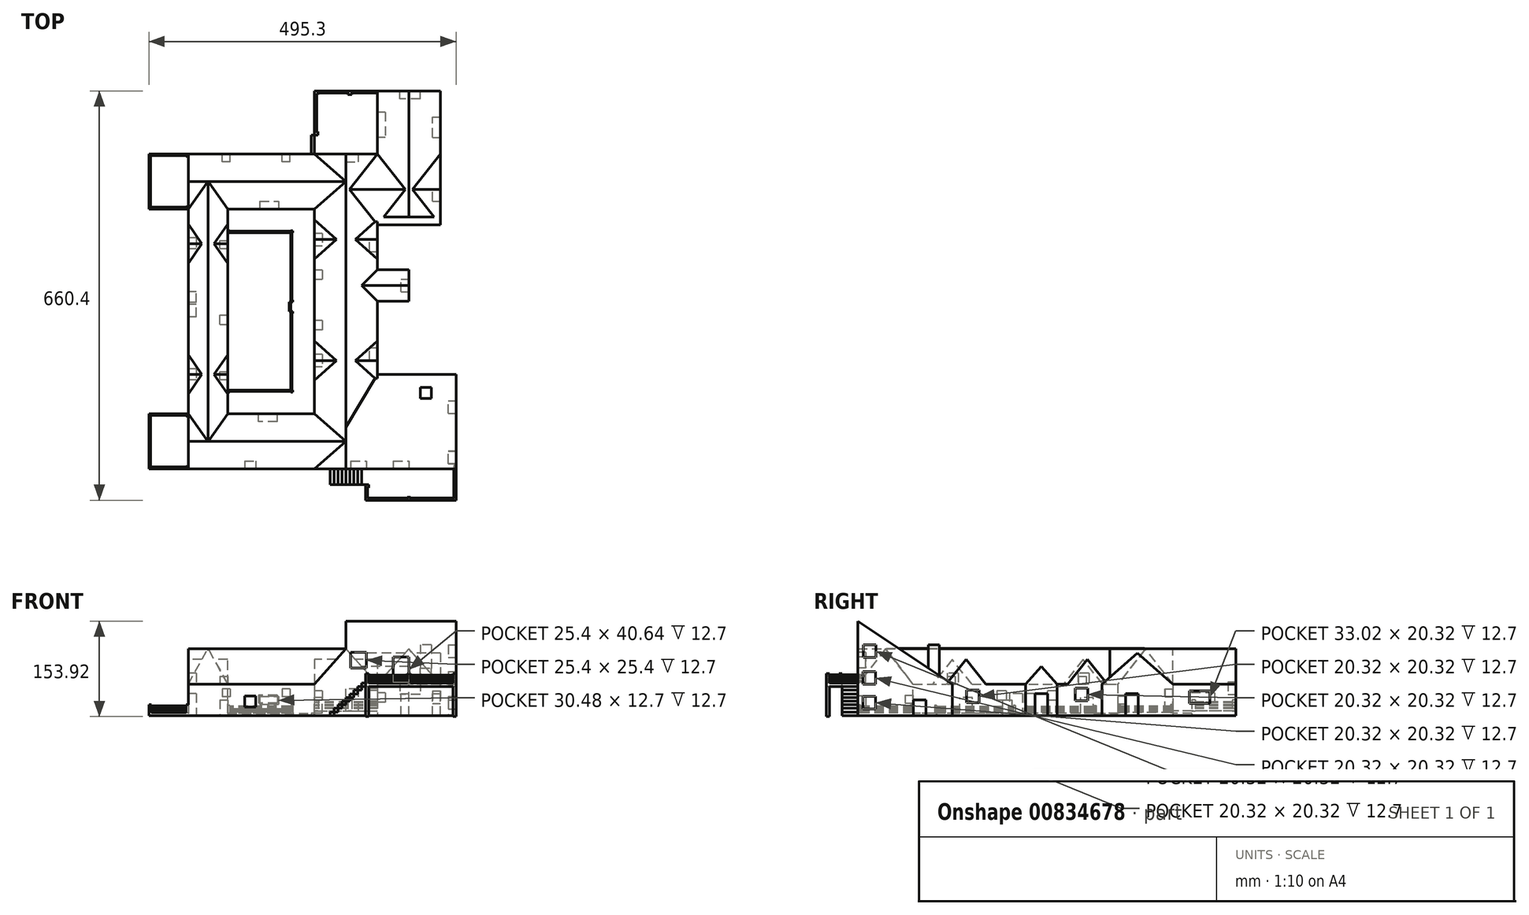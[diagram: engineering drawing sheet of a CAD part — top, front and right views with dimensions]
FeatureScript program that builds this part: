
annotation { "Feature Type Name" : "Feature", "Feature Type Description" : "" }
export const myFeature = defineFeature(function(context is Context, id is Id, definition is map)
    precondition{}
    {
        {
            var Q0;
            Q0=qCreatedBy(makeId("Front.planeOp"),FACE);
            var sketch = newSketch(context, id + "F0", { "sketchPlane" : qUnion([Q0])});
            skLineSegment(sketch, "E0", {"start": v(-50.8, -50.8) * mm, "end": v(50.8, -50.8) * mm});
            skLineSegment(sketch, "E1", {"start": v(50.8, -50.8) * mm, "end": v(50.8, 0) * mm});
            skLineSegment(sketch, "E2", {"start": v(50.8, 0) * mm, "end": v(-50.8, 0) * mm});
            skLineSegment(sketch, "E3", {"start": v(-50.8, 0) * mm, "end": v(-50.8, -50.8) * mm});
            skLineSegment(sketch, "E4", {"start": v(-50.8, 0) * mm, "end": v(0, 56.8) * mm});
            skLineSegment(sketch, "E5", {"start": v(0, 56.8) * mm, "end": v(50.8, 0) * mm});
            skSolve(sketch);
        }
        {
            var Q0;
            Q0=makeQuery(id+"F0.imprint","IMPRINT",FACE,{"disambiguationData":[TD([[makeQuery(id+"F0.imprint","IMPRINT",EDGE,{"derivedFrom":sQuery(id+"F0.wireOp",EDGE,"E2")}),-1.0]])]});
            var Q1;
            Q1=makeQuery(id+"F0.imprint","IMPRINT",FACE,{"disambiguationData":[TD([[makeQuery(id+"F0.imprint","IMPRINT",EDGE,{"derivedFrom":sQuery(id+"F0.wireOp",EDGE,"E0")}),1.0]])]});
            extrude(context, id + "F1", {"entities" : qUnion([Q0, Q1]), "depth" : 508 * mm, "offsetDistance" : 25.4 * mm});
        }
        {
            var Q0;
            Q0=makeQuery(id+"F1.opExtrude","SWEPT_FACE",FACE,{"disambiguationData":[OSD([sQuery(id+"F0.wireOp",EDGE,"E1")])]});
            var sketch = newSketch(context, id + "F2", { "sketchPlane" : qUnion([Q0])});
            skLineSegment(sketch, "E6", {"start": v(-355.6, 0) * mm, "end": v(-508, 0) * mm});
            skLineSegment(sketch, "E7", {"start": v(-355.6, 0) * mm, "end": v(-355.6, -50.8) * mm});
            skLineSegment(sketch, "E8", {"start": v(-355.6, -50.8) * mm, "end": v(-508, -50.8) * mm});
            skLineSegment(sketch, "E9", {"start": v(-508, -50.8) * mm, "end": v(-508, 0) * mm});
            skLineSegment(sketch, "E10", {"start": v(-508, 0) * mm, "end": v(-508, 101.6) * mm});
            skLineSegment(sketch, "E11", {"start": v(-508, 101.6) * mm, "end": v(-355.6, 0) * mm});
            skSolve(sketch);
        }
        {
            var Q0;
            Q0=makeQuery(id+"F2.imprint","IMPRINT",FACE,{"disambiguationData":[TD([[makeQuery(id+"F2.imprint","IMPRINT",EDGE,{"derivedFrom":sQuery(id+"F2.wireOp",EDGE,"E6")}),-1.0]])]});
            var Q1;
            Q1=makeQuery(id+"F2.imprint","IMPRINT",FACE,{"disambiguationData":[TD([[makeQuery(id+"F2.imprint","IMPRINT",EDGE,{"derivedFrom":sQuery(id+"F2.wireOp",EDGE,"iOD2iBbH-JStM-AViZ-ixR9-aIs0KOxaWcK1")}),-1.0]])]});
            extrude(context, id + "F3", {"entities" : qUnion([Q0, Q1]), "operationType" : NewBodyOperationType.ADD, "depth" : 127 * mm, "offsetDistance" : 25.4 * mm});
        }
        {
            var Q0;
            Q0=makeQuery(id+"F2.imprint","IMPRINT",FACE,{"disambiguationData":[TD([[makeQuery(id+"F2.imprint","IMPRINT",EDGE,{"derivedFrom":sQuery(id+"F2.wireOp",EDGE,"E6")}),1.0]])]});
            extrude(context, id + "F4", {"entities" : qUnion([Q0]), "operationType" : NewBodyOperationType.ADD, "depth" : 127 * mm, "offsetDistance" : 25.4 * mm});
        }
        {
            var Q0;
            Q0=makeQuery(id+"F4.opExtrude","CAP_FACE",FACE,{"disambiguationData":[OSD([sQuery(id+"F2.wireOp",EDGE,"E6"),sQuery(id+"F2.wireOp",EDGE,"E10"),sQuery(id+"F2.wireOp",EDGE,"E11")])],"isStart":true});
            extrude(context, id + "F5", {"entities" : qUnion([Q0]), "operationType" : NewBodyOperationType.ADD, "depth" : 50.8 * mm, "offsetDistance" : 25.4 * mm});
        }
        {
            var Q0;
            Q0=makeQuery(id+"F1.opExtrude","SWEPT_FACE",FACE,{"disambiguationData":[OSD([sQuery(id+"F0.wireOp",EDGE,"E1")])]});
            var sketch = newSketch(context, id + "F6", { "sketchPlane" : qUnion([Q0])});
            skLineSegment(sketch, "E12.bottom", {"start": v(-237.52, -50.8) * mm, "end": v(-186.72, -50.8) * mm});
            skLineSegment(sketch, "E12.top", {"start": v(-237.52, 0) * mm, "end": v(-186.72, 0) * mm});
            skLineSegment(sketch, "E12.left", {"start": v(-237.52, -50.8) * mm, "end": v(-237.52, 0) * mm});
            skLineSegment(sketch, "E12.right", {"start": v(-186.72, -50.8) * mm, "end": v(-186.72, 0) * mm});
            skLineSegment(sketch, "E13", {"start": v(-237.52, 0) * mm, "end": v(-212.12, 28.4) * mm});
            skPoint(sketch, "E13.endSnap0", {"position": v(-212.12, 0) * mm});
            skLineSegment(sketch, "E14", {"start": v(-212.12, 28.4) * mm, "end": v(-186.72, 0) * mm});
            skSolve(sketch);
        }
        {
            var Q0;
            Q0=makeQuery(id+"F6.imprint","IMPRINT",FACE,{"disambiguationData":[TD([[makeQuery(id+"F6.imprint","IMPRINT",EDGE,{"derivedFrom":sQuery(id+"F6.wireOp",EDGE,"E12.bottom")}),1.0]])]});
            var Q1;
            Q1=makeQuery(id+"F6.imprint","IMPRINT",FACE,{"disambiguationData":[TD([[makeQuery(id+"F6.imprint","IMPRINT",EDGE,{"derivedFrom":sQuery(id+"F6.wireOp",EDGE,"E12.top")}),1.0]])]});
            extrude(context, id + "F7", {"entities" : qUnion([Q0, Q1]), "operationType" : NewBodyOperationType.ADD, "depth" : 50.8 * mm, "offsetDistance" : 25.4 * mm});
        }
        {
            var Q0;
            Q0=makeQuery(id+"F7.opExtrude","CAP_FACE",FACE,{"disambiguationData":[OSD([sQuery(id+"F6.wireOp",EDGE,"E12.bottom"),sQuery(id+"F6.wireOp",EDGE,"E12.left"),sQuery(id+"F6.wireOp",EDGE,"E12.right"),sQuery(id+"F6.wireOp",EDGE,"E13"),sQuery(id+"F6.wireOp",EDGE,"E14")])],"isStart":true});
            extrude(context, id + "F8", {"entities" : qUnion([Q0]), "operationType" : NewBodyOperationType.ADD, "depth" : 25.4 * mm, "offsetDistance" : 25.4 * mm});
        }
        {
            var Q0;
            {var subQ2=sQuery(id+"F0.wireOp",EDGE,"E1");var subQ4=sQuery(id+"F6.wireOp",EDGE,"E12.right");Q0=makeQuery(id+"F7.boolean.opBoolean","SPLIT",FACE,{"disambiguationData":[TD([makeQuery(id+"F7.opExtrude","SWEPT_FACE",FACE,{"disambiguationData":[OSD([subQ4])]})])],"derivedFrom":makeQuery(id+"F1.opExtrude","SWEPT_FACE",FACE,{"disambiguationData":[OSD([subQ2])]})});}
            var sketch = newSketch(context, id + "F9", { "sketchPlane" : qUnion([Q0])});
            skLineSegment(sketch, "E15.bottom", {"start": v(-114.3, 0) * mm, "end": v(0, 0) * mm});
            skLineSegment(sketch, "E15.top", {"start": v(-114.3, -50.8) * mm, "end": v(0, -50.8) * mm});
            skLineSegment(sketch, "E15.left", {"start": v(-114.3, 0) * mm, "end": v(-114.3, -50.8) * mm});
            skLineSegment(sketch, "E15.right", {"start": v(0, 0) * mm, "end": v(0, -50.8) * mm});
            skLineSegment(sketch, "E16", {"start": v(-114.3, 0) * mm, "end": v(-57.15, 50.4) * mm});
            skPoint(sketch, "E16.endSnap0", {"position": v(-57.15, 0) * mm});
            skLineSegment(sketch, "E17", {"start": v(-57.15, 50.4) * mm, "end": v(0, 0) * mm});
            skSolve(sketch);
        }
        {
            var Q0;
            Q0=makeQuery(id+"F9.imprint","IMPRINT",FACE,{"disambiguationData":[TD([[makeQuery(id+"F9.imprint","IMPRINT",EDGE,{"derivedFrom":sQuery(id+"F9.wireOp",EDGE,"E15.bottom")}),1.0]])]});
            var Q1;
            Q1=makeQuery(id+"F9.imprint","IMPRINT",FACE,{"disambiguationData":[TD([[makeQuery(id+"F9.imprint","IMPRINT",EDGE,{"derivedFrom":sQuery(id+"F9.wireOp",EDGE,"E15.bottom")}),-1.0]])]});
            extrude(context, id + "F10", {"entities" : qUnion([Q0, Q1]), "operationType" : NewBodyOperationType.ADD, "depth" : 101.6 * mm, "offsetDistance" : 25.4 * mm});
        }
        {
            var Q0;
            Q0=makeQuery(id+"F10.opExtrude","CAP_FACE",FACE,{"disambiguationData":[OSD([sQuery(id+"F9.wireOp",EDGE,"E15.top"),sQuery(id+"F9.wireOp",EDGE,"E15.left"),sQuery(id+"F9.wireOp",EDGE,"E15.right"),sQuery(id+"F9.wireOp",EDGE,"E16"),sQuery(id+"F9.wireOp",EDGE,"E17")])],"isStart":true});
            extrude(context, id + "F11", {"entities" : qUnion([Q0]), "operationType" : NewBodyOperationType.ADD, "depth" : 50.8 * mm, "offsetDistance" : 25.4 * mm});
        }
        {
            var Q0;
            Q0=makeQuery(id+"F10.boolean.opBoolean","MERGE",FACE,{"derivedFrom":[makeQuery(id+"F1.opExtrude","CAP_FACE",FACE,{"disambiguationData":[OSD([sQuery(id+"F0.wireOp",EDGE,"E0"),sQuery(id+"F0.wireOp",EDGE,"E1"),sQuery(id+"F0.wireOp",EDGE,"E3"),sQuery(id+"F0.wireOp",EDGE,"E4"),sQuery(id+"F0.wireOp",EDGE,"E5")])],"isStart":true}),makeQuery(id+"F10.opExtrude","SWEPT_FACE",FACE,{"disambiguationData":[OSD([sQuery(id+"F9.wireOp",EDGE,"E15.right")])]})]});
            var sketch = newSketch(context, id + "F12", { "sketchPlane" : qUnion([Q0])});
            skLineSegment(sketch, "E18.bottom", {"start": v(-50.8, 0) * mm, "end": v(-152.4, 0) * mm});
            skLineSegment(sketch, "E18.top", {"start": v(-50.8, -50.8) * mm, "end": v(-152.4, -50.8) * mm});
            skLineSegment(sketch, "E18.left", {"start": v(-50.8, 0) * mm, "end": v(-50.8, -50.8) * mm});
            skLineSegment(sketch, "E18.right", {"start": v(-152.4, 0) * mm, "end": v(-152.4, -50.8) * mm});
            skLineSegment(sketch, "E19", {"start": v(-152.4, 0) * mm, "end": v(-101.6, 56.8) * mm});
            skPoint(sketch, "E19.endSnap0", {"position": v(-101.6, 0) * mm});
            skLineSegment(sketch, "E20", {"start": v(-101.6, 56.8) * mm, "end": v(-50.8, 0) * mm});
            skSolve(sketch);
        }
        {
            var Q0;
            Q0=makeQuery(id+"F12.imprint","IMPRINT",FACE,{"disambiguationData":[TD([[makeQuery(id+"F12.imprint","IMPRINT",EDGE,{"derivedFrom":sQuery(id+"F12.wireOp",EDGE,"E18.bottom")}),-1.0]])]});
            var Q1;
            Q1=makeQuery(id+"F12.imprint","IMPRINT",FACE,{"disambiguationData":[TD([[makeQuery(id+"F12.imprint","IMPRINT",EDGE,{"derivedFrom":sQuery(id+"F12.wireOp",EDGE,"E18.bottom")}),1.0]])]});
            extrude(context, id + "F13", {"entities" : qUnion([Q0, Q1]), "operationType" : NewBodyOperationType.ADD, "depth" : 101.6 * mm, "offsetDistance" : 25.4 * mm});
        }
        {
            var Q0;
            Q0=makeQuery(id+"F13.opExtrude","CAP_FACE",FACE,{"disambiguationData":[OSD([sQuery(id+"F12.wireOp",EDGE,"E18.top"),sQuery(id+"F12.wireOp",EDGE,"E18.left"),sQuery(id+"F12.wireOp",EDGE,"E18.right"),sQuery(id+"F12.wireOp",EDGE,"E19"),sQuery(id+"F12.wireOp",EDGE,"E20")])],"isStart":true});
            extrude(context, id + "F14", {"entities" : qUnion([Q0]), "operationType" : NewBodyOperationType.ADD, "depth" : 101.6 * mm, "offsetDistance" : 25.4 * mm});
        }
        {
            var Q0;
            Q0=makeQuery(id+"F1.opExtrude","SWEPT_FACE",FACE,{"disambiguationData":[OSD([sQuery(id+"F0.wireOp",EDGE,"E3")])]});
            var sketch = newSketch(context, id + "F15", { "sketchPlane" : qUnion([Q0])});
            skLineSegment(sketch, "E21.bottom", {"start": v(0, 0) * mm, "end": v(88.9, 0) * mm});
            skLineSegment(sketch, "E21.top", {"start": v(0, -50.8) * mm, "end": v(88.9, -50.8) * mm});
            skLineSegment(sketch, "E21.left", {"start": v(0, 0) * mm, "end": v(0, -50.8) * mm});
            skLineSegment(sketch, "E21.right", {"start": v(88.9, 0) * mm, "end": v(88.9, -50.8) * mm});
            skLineSegment(sketch, "E22", {"start": v(0, 0) * mm, "end": v(44.45, 56.81) * mm});
            skPoint(sketch, "E22.endSnap0", {"position": v(44.45, 0) * mm});
            skLineSegment(sketch, "E23", {"start": v(44.45, 56.81) * mm, "end": v(88.9, 0) * mm});
            skLineSegment(sketch, "E24.bottom", {"start": v(508, 0) * mm, "end": v(419.1, 0) * mm});
            skLineSegment(sketch, "E24.top", {"start": v(508, -50.8) * mm, "end": v(419.1, -50.8) * mm});
            skLineSegment(sketch, "E24.left", {"start": v(508, 0) * mm, "end": v(508, -50.8) * mm});
            skLineSegment(sketch, "E24.right", {"start": v(419.1, 0) * mm, "end": v(419.1, -50.8) * mm});
            skLineSegment(sketch, "E25", {"start": v(419.1, 0) * mm, "end": v(463.55, 56.81) * mm});
            skPoint(sketch, "E25.endSnap0", {"position": v(463.55, 0) * mm});
            skLineSegment(sketch, "E26", {"start": v(463.55, 56.81) * mm, "end": v(508, 0) * mm});
            skSolve(sketch);
        }
        {
            var Q0;
            Q0=makeQuery(id+"F15.imprint","IMPRINT",FACE,{"disambiguationData":[TD([[makeQuery(id+"F15.imprint","IMPRINT",EDGE,{"derivedFrom":sQuery(id+"F15.wireOp",EDGE,"E21.bottom")}),1.0]])]});
            var Q1;
            Q1=makeQuery(id+"F15.imprint","IMPRINT",FACE,{"disambiguationData":[TD([[makeQuery(id+"F15.imprint","IMPRINT",EDGE,{"derivedFrom":sQuery(id+"F15.wireOp",EDGE,"E21.bottom")}),-1.0]])]});
            var Q2;
            Q2=makeQuery(id+"F15.imprint","IMPRINT",FACE,{"disambiguationData":[TD([[makeQuery(id+"F15.imprint","IMPRINT",EDGE,{"derivedFrom":sQuery(id+"F15.wireOp",EDGE,"E24.bottom")}),1.0]])]});
            var Q3;
            Q3=makeQuery(id+"F15.imprint","IMPRINT",FACE,{"disambiguationData":[TD([[makeQuery(id+"F15.imprint","IMPRINT",EDGE,{"derivedFrom":sQuery(id+"F15.wireOp",EDGE,"E24.bottom")}),-1.0]])]});
            extrude(context, id + "F16", {"entities" : qUnion([Q0, Q1, Q2, Q3]), "operationType" : NewBodyOperationType.ADD, "depth" : 203.2 * mm, "offsetDistance" : 25.4 * mm});
        }
        {
            var Q0;
            Q0=makeQuery(id+"F16.opExtrude","CAP_FACE",FACE,{"disambiguationData":[OSD([sQuery(id+"F15.wireOp",EDGE,"E21.top"),sQuery(id+"F15.wireOp",EDGE,"E21.left"),sQuery(id+"F15.wireOp",EDGE,"E21.right"),sQuery(id+"F15.wireOp",EDGE,"E22"),sQuery(id+"F15.wireOp",EDGE,"E23")])],"isStart":true});
            extrude(context, id + "F17", {"entities" : qUnion([Q0]), "operationType" : NewBodyOperationType.ADD, "depth" : 50.8 * mm, "offsetDistance" : 25.4 * mm});
        }
        {
            var Q0;
            Q0=makeQuery(id+"F16.opExtrude","CAP_FACE",FACE,{"disambiguationData":[OSD([sQuery(id+"F15.wireOp",EDGE,"E24.top"),sQuery(id+"F15.wireOp",EDGE,"E24.left"),sQuery(id+"F15.wireOp",EDGE,"E24.right"),sQuery(id+"F15.wireOp",EDGE,"E25"),sQuery(id+"F15.wireOp",EDGE,"E26")])],"isStart":true});
            extrude(context, id + "F18", {"entities" : qUnion([Q0]), "operationType" : NewBodyOperationType.ADD, "depth" : 50.8 * mm, "offsetDistance" : 25.4 * mm});
        }
        {
            var Q0;
            Q0=makeQuery(id+"F16.opExtrude","SWEPT_FACE",FACE,{"disambiguationData":[OSD([sQuery(id+"F15.wireOp",EDGE,"E21.right")])]});
            var sketch = newSketch(context, id + "F19", { "sketchPlane" : qUnion([Q0])});
            skLineSegment(sketch, "E27.bottom", {"start": v(-190.5, 0) * mm, "end": v(-254, 0) * mm});
            skLineSegment(sketch, "E27.top", {"start": v(-190.5, -50.8) * mm, "end": v(-254, -50.8) * mm});
            skLineSegment(sketch, "E27.left", {"start": v(-190.5, 0) * mm, "end": v(-190.5, -50.8) * mm});
            skLineSegment(sketch, "E27.right", {"start": v(-254, 0) * mm, "end": v(-254, -50.8) * mm});
            skLineSegment(sketch, "E28", {"start": v(-254, 0) * mm, "end": v(-222.25, 57.62) * mm});
            skPoint(sketch, "E28.endSnap0", {"position": v(-222.25, 0) * mm});
            skLineSegment(sketch, "E29", {"start": v(-222.25, 57.62) * mm, "end": v(-190.5, 0) * mm});
            skSolve(sketch);
        }
        {
            var Q0;
            Q0=makeQuery(id+"F19.imprint","IMPRINT",FACE,{"disambiguationData":[TD([[makeQuery(id+"F19.imprint","IMPRINT",EDGE,{"derivedFrom":sQuery(id+"F19.wireOp",EDGE,"E27.bottom")}),-1.0]])]});
            var Q1;
            Q1=makeQuery(id+"F19.imprint","IMPRINT",FACE,{"disambiguationData":[TD([[makeQuery(id+"F19.imprint","IMPRINT",EDGE,{"derivedFrom":sQuery(id+"F19.wireOp",EDGE,"E27.bottom")}),1.0]])]});
            extrude(context, id + "F20", {"entities" : qUnion([Q0, Q1]), "operationType" : NewBodyOperationType.ADD, "depth" : 355.6 * mm, "offsetDistance" : 25.4 * mm});
        }
        {
            var Q0;
            Q0=makeQuery(id+"F20.opExtrude","CAP_FACE",FACE,{"disambiguationData":[OSD([sQuery(id+"F19.wireOp",EDGE,"E27.top"),sQuery(id+"F19.wireOp",EDGE,"E27.left"),sQuery(id+"F19.wireOp",EDGE,"E27.right"),sQuery(id+"F19.wireOp",EDGE,"E28"),sQuery(id+"F19.wireOp",EDGE,"E29")])],"isStart":false});
            extrude(context, id + "F21", {"entities" : qUnion([Q0]), "operationType" : NewBodyOperationType.ADD, "depth" : 17.78 * mm, "offsetDistance" : 25.4 * mm});
        }
        {
            var Q0;
            Q0=makeQuery(id+"F20.opExtrude","CAP_FACE",FACE,{"disambiguationData":[OSD([sQuery(id+"F19.wireOp",EDGE,"E27.top"),sQuery(id+"F19.wireOp",EDGE,"E27.left"),sQuery(id+"F19.wireOp",EDGE,"E27.right"),sQuery(id+"F19.wireOp",EDGE,"E28"),sQuery(id+"F19.wireOp",EDGE,"E29")])],"isStart":true});
            extrude(context, id + "F22", {"entities" : qUnion([Q0]), "operationType" : NewBodyOperationType.ADD, "depth" : 43.18 * mm, "offsetDistance" : 25.4 * mm});
        }
        {
            var Q0;
            Q0=makeQuery(id+"F1.opExtrude","SWEPT_FACE",FACE,{"disambiguationData":[OSD([sQuery(id+"F0.wireOp",EDGE,"E3")])]});
            var sketch = newSketch(context, id + "F23", { "sketchPlane" : qUnion([Q0])});
            skLineSegment(sketch, "E30", {"start": v(106.35, 0) * mm, "end": v(138.1, 39.66) * mm});
            skLineSegment(sketch, "E31", {"start": v(138.1, 39.66) * mm, "end": v(169.85, 0) * mm});
            skLineSegment(sketch, "E32", {"start": v(169.85, 0) * mm, "end": v(106.35, 0) * mm});
            skLineSegment(sketch, "E33", {"start": v(301.86, 0) * mm, "end": v(333.61, 39.66) * mm});
            skLineSegment(sketch, "E34", {"start": v(333.61, 39.66) * mm, "end": v(365.36, 0) * mm});
            skLineSegment(sketch, "E35", {"start": v(365.36, 0) * mm, "end": v(301.86, 0) * mm});
            skSolve(sketch);
        }
        {
            var Q0;
            Q0=makeQuery(id+"F23.imprint","IMPRINT",FACE,{"disambiguationData":[TD([[makeQuery(id+"F23.imprint","IMPRINT",EDGE,{"derivedFrom":sQuery(id+"F23.wireOp",EDGE,"E30")}),-1.0]])]});
            var Q1;
            Q1=makeQuery(id+"F23.imprint","IMPRINT",FACE,{"disambiguationData":[TD([[makeQuery(id+"F23.imprint","IMPRINT",EDGE,{"derivedFrom":sQuery(id+"F23.wireOp",EDGE,"E33")}),-1.0]])]});
            extrude(context, id + "F24", {"entities" : qUnion([Q0, Q1]), "operationType" : NewBodyOperationType.ADD, "oppositeDirection" : true, "depth" : 101.6 * mm, "offsetDistance" : 25.4 * mm});
        }
        {
            var Q0;
            Q0=makeQuery(id+"F20.boolean.opBoolean","MERGE",FACE,{"derivedFrom":[makeQuery(id+"F16.opExtrude","CAP_FACE",FACE,{"disambiguationData":[OSD([sQuery(id+"F15.wireOp",EDGE,"E21.top"),sQuery(id+"F15.wireOp",EDGE,"E21.left"),sQuery(id+"F15.wireOp",EDGE,"E21.right"),sQuery(id+"F15.wireOp",EDGE,"E22"),sQuery(id+"F15.wireOp",EDGE,"E23")])],"isStart":false}),makeQuery(id+"F16.opExtrude","CAP_FACE",FACE,{"disambiguationData":[OSD([sQuery(id+"F15.wireOp",EDGE,"E24.top"),sQuery(id+"F15.wireOp",EDGE,"E24.left"),sQuery(id+"F15.wireOp",EDGE,"E24.right"),sQuery(id+"F15.wireOp",EDGE,"E25"),sQuery(id+"F15.wireOp",EDGE,"E26")])],"isStart":false}),makeQuery(id+"F20.opExtrude","SWEPT_FACE",FACE,{"disambiguationData":[OSD([sQuery(id+"F19.wireOp",EDGE,"E27.right")])]})]});
            var sketch = newSketch(context, id + "F25", { "sketchPlane" : qUnion([Q0])});
            skLineSegment(sketch, "E36", {"start": v(113.08, 0) * mm, "end": v(144.83, 39.66) * mm});
            skLineSegment(sketch, "E37", {"start": v(144.83, 39.66) * mm, "end": v(176.58, 0) * mm});
            skLineSegment(sketch, "E38", {"start": v(176.58, 0) * mm, "end": v(113.08, 0) * mm});
            skLineSegment(sketch, "E39", {"start": v(324.16, 0) * mm, "end": v(355.91, 39.66) * mm});
            skLineSegment(sketch, "E40", {"start": v(355.91, 39.66) * mm, "end": v(387.66, 0) * mm});
            skLineSegment(sketch, "E41", {"start": v(387.66, 0) * mm, "end": v(324.16, 0) * mm});
            skSolve(sketch);
        }
        {
            var Q0;
            Q0=makeQuery(id+"F25.imprint","IMPRINT",FACE,{"disambiguationData":[TD([[makeQuery(id+"F25.imprint","IMPRINT",EDGE,{"derivedFrom":sQuery(id+"F25.wireOp",EDGE,"E36")}),-1.0]])]});
            var Q1;
            Q1=makeQuery(id+"F25.imprint","IMPRINT",FACE,{"disambiguationData":[TD([[makeQuery(id+"F25.imprint","IMPRINT",EDGE,{"derivedFrom":sQuery(id+"F25.wireOp",EDGE,"E39")}),-1.0]])]});
            extrude(context, id + "F26", {"entities" : qUnion([Q0, Q1]), "operationType" : NewBodyOperationType.ADD, "oppositeDirection" : true, "depth" : 63.5 * mm, "offsetDistance" : 25.4 * mm});
        }
        {
            var Q0;
            Q0=makeQuery(id+"F13.opExtrude","SWEPT_FACE",FACE,{"disambiguationData":[OSD([sQuery(id+"F12.wireOp",EDGE,"E18.left")])]});
            var sketch = newSketch(context, id + "F27", { "sketchPlane" : qUnion([Q0])});
            skLineSegment(sketch, "E42.bottom", {"start": v(-101.6, -43.18) * mm, "end": v(0, -43.18) * mm});
            skLineSegment(sketch, "E42.top", {"start": v(-101.6, -50.8) * mm, "end": v(0, -50.8) * mm});
            skLineSegment(sketch, "E42.left", {"start": v(-101.6, -43.18) * mm, "end": v(-101.6, -50.8) * mm});
            skLineSegment(sketch, "E42.right", {"start": v(0, -43.18) * mm, "end": v(0, -50.8) * mm});
            skSolve(sketch);
        }
        {
            var Q0;
            Q0=makeQuery(id+"F27.imprint","IMPRINT",FACE,{"disambiguationData":[TD([[makeQuery(id+"F27.imprint","IMPRINT",EDGE,{"derivedFrom":sQuery(id+"F27.wireOp",EDGE,"E42.bottom")}),-1.0]])]});
            extrude(context, id + "F28", {"entities" : qUnion([Q0]), "operationType" : NewBodyOperationType.ADD, "depth" : 101.6 * mm, "offsetDistance" : 25.4 * mm});
        }
        {
            var Q0;
            Q0=makeQuery(id+"F28.opExtrude","SWEPT_FACE",FACE,{"disambiguationData":[OSD([sQuery(id+"F27.wireOp",EDGE,"E42.bottom")])]});
            var sketch = newSketch(context, id + "F29", { "sketchPlane" : qUnion([Q0])});
            skLineSegment(sketch, "E43.bottom", {"start": v(-44.7, 101.6) * mm, "end": v(-50.8, 101.6) * mm});
            skLineSegment(sketch, "E43.top", {"start": v(-44.7, 96.01) * mm, "end": v(-50.8, 96.01) * mm});
            skLineSegment(sketch, "E43.left", {"start": v(-44.7, 101.6) * mm, "end": v(-44.7, 96.01) * mm});
            skLineSegment(sketch, "E43.right", {"start": v(-50.8, 101.6) * mm, "end": v(-50.8, 96.01) * mm});
            skLineSegment(sketch, "E44.bottom", {"start": v(-50.8, 30.52) * mm, "end": v(-44.7, 30.52) * mm});
            skLineSegment(sketch, "E44.top", {"start": v(-50.8, 36.1) * mm, "end": v(-44.7, 36.1) * mm});
            skLineSegment(sketch, "E44.left", {"start": v(-50.8, 30.52) * mm, "end": v(-50.8, 36.1) * mm});
            skLineSegment(sketch, "E44.right", {"start": v(-44.7, 30.52) * mm, "end": v(-44.7, 36.1) * mm});
            skLineSegment(sketch, "E45.bottom", {"start": v(9.73, 96.01) * mm, "end": v(3.63, 96.01) * mm});
            skLineSegment(sketch, "E45.top", {"start": v(9.73, 101.6) * mm, "end": v(3.63, 101.6) * mm});
            skLineSegment(sketch, "E45.left", {"start": v(9.73, 96.01) * mm, "end": v(9.73, 101.6) * mm});
            skLineSegment(sketch, "E45.right", {"start": v(3.63, 96.01) * mm, "end": v(3.63, 101.6) * mm});
            skSolve(sketch);
        }
        {
            var Q0;
            Q0=makeQuery(id+"F29.imprint","IMPRINT",FACE,{"disambiguationData":[TD([[makeQuery(id+"F29.imprint","IMPRINT",EDGE,{"derivedFrom":sQuery(id+"F29.wireOp",EDGE,"E44.bottom")}),1.0]])]});
            var Q1;
            Q1=makeQuery(id+"F29.imprint","IMPRINT",FACE,{"disambiguationData":[TD([[makeQuery(id+"F29.imprint","IMPRINT",EDGE,{"derivedFrom":sQuery(id+"F29.wireOp",EDGE,"E43.bottom")}),-1.0]])]});
            var Q2;
            Q2=makeQuery(id+"F29.imprint","IMPRINT",FACE,{"disambiguationData":[TD([[makeQuery(id+"F29.imprint","IMPRINT",EDGE,{"derivedFrom":sQuery(id+"F29.wireOp",EDGE,"E45.bottom")}),-1.0]])]});
            extrude(context, id + "F30", {"entities" : qUnion([Q0, Q1, Q2]), "operationType" : NewBodyOperationType.ADD, "depth" : 17.78 * mm, "offsetDistance" : 25.4 * mm});
        }
        {
            var Q0;
            Q0=makeQuery(id+"F30.opExtrude","SWEPT_FACE",FACE,{"disambiguationData":[OSD([sQuery(id+"F29.wireOp",EDGE,"E44.top")])]});
            var sketch = newSketch(context, id + "F31", { "sketchPlane" : qUnion([Q0])});
            skLineSegment(sketch, "E46.bottom", {"start": v(46.74, -28.7) * mm, "end": v(48.26, -28.7) * mm});
            skLineSegment(sketch, "E46.top", {"start": v(46.74, -30.1) * mm, "end": v(48.26, -30.1) * mm});
            skLineSegment(sketch, "E46.left", {"start": v(46.74, -28.7) * mm, "end": v(46.74, -30.1) * mm});
            skLineSegment(sketch, "E46.right", {"start": v(48.26, -28.7) * mm, "end": v(48.26, -30.1) * mm});
            skLineSegment(sketch, "E47.bottom", {"start": v(46.74, -33.4) * mm, "end": v(48.26, -33.4) * mm});
            skLineSegment(sketch, "E47.top", {"start": v(46.74, -34.8) * mm, "end": v(48.26, -34.8) * mm});
            skLineSegment(sketch, "E47.left", {"start": v(46.74, -33.4) * mm, "end": v(46.74, -34.8) * mm});
            skLineSegment(sketch, "E47.right", {"start": v(48.26, -33.4) * mm, "end": v(48.26, -34.8) * mm});
            skLineSegment(sketch, "E48.bottom", {"start": v(46.74, -38.1) * mm, "end": v(48.26, -38.1) * mm});
            skLineSegment(sketch, "E48.top", {"start": v(46.74, -39.5) * mm, "end": v(48.26, -39.5) * mm});
            skLineSegment(sketch, "E48.left", {"start": v(46.74, -38.1) * mm, "end": v(46.74, -39.5) * mm});
            skLineSegment(sketch, "E48.right", {"start": v(48.26, -38.1) * mm, "end": v(48.26, -39.5) * mm});
            skSolve(sketch);
        }
        {
            var Q0;
            Q0=makeQuery(id+"F31.imprint","IMPRINT",FACE,{"disambiguationData":[TD([[makeQuery(id+"F31.imprint","IMPRINT",EDGE,{"derivedFrom":sQuery(id+"F31.wireOp",EDGE,"E48.bottom")}),-1.0]])]});
            var Q1;
            Q1=makeQuery(id+"F31.imprint","IMPRINT",FACE,{"disambiguationData":[TD([[makeQuery(id+"F31.imprint","IMPRINT",EDGE,{"derivedFrom":sQuery(id+"F31.wireOp",EDGE,"E47.bottom")}),-1.0]])]});
            var Q2;
            Q2=makeQuery(id+"F31.imprint","IMPRINT",FACE,{"disambiguationData":[TD([[makeQuery(id+"F31.imprint","IMPRINT",EDGE,{"derivedFrom":sQuery(id+"F31.wireOp",EDGE,"E46.bottom")}),-1.0]])]});
            extrude(context, id + "F32", {"entities" : qUnion([Q0, Q1, Q2]), "operationType" : NewBodyOperationType.ADD, "depth" : 63.5 * mm, "offsetDistance" : 25.4 * mm});
        }
        {
            var Q0;
            Q0=makeQuery(id+"F30.opExtrude","SWEPT_FACE",FACE,{"disambiguationData":[OSD([sQuery(id+"F29.wireOp",EDGE,"E43.left")])]});
            var sketch = newSketch(context, id + "F33", { "sketchPlane" : qUnion([Q0])});
            skLineSegment(sketch, "E49.bottom", {"start": v(98.04, -33.4) * mm, "end": v(99.57, -33.4) * mm});
            skLineSegment(sketch, "E49.top", {"start": v(98.04, -34.8) * mm, "end": v(99.57, -34.8) * mm});
            skLineSegment(sketch, "E49.left", {"start": v(98.04, -33.4) * mm, "end": v(98.04, -34.8) * mm});
            skLineSegment(sketch, "E49.right", {"start": v(99.57, -33.4) * mm, "end": v(99.57, -34.8) * mm});
            skLineSegment(sketch, "E50.bottom", {"start": v(98.04, -38.1) * mm, "end": v(99.57, -38.1) * mm});
            skLineSegment(sketch, "E50.top", {"start": v(98.04, -39.5) * mm, "end": v(99.57, -39.5) * mm});
            skLineSegment(sketch, "E50.left", {"start": v(98.04, -38.1) * mm, "end": v(98.04, -39.5) * mm});
            skLineSegment(sketch, "E50.right", {"start": v(99.57, -38.1) * mm, "end": v(99.57, -39.5) * mm});
            skLineSegment(sketch, "E51.bottom", {"start": v(98.04, -28.7) * mm, "end": v(99.57, -28.7) * mm});
            skLineSegment(sketch, "E51.top", {"start": v(98.04, -30.1) * mm, "end": v(99.57, -30.1) * mm});
            skLineSegment(sketch, "E51.left", {"start": v(98.04, -28.7) * mm, "end": v(98.04, -30.1) * mm});
            skLineSegment(sketch, "E51.right", {"start": v(99.57, -28.7) * mm, "end": v(99.57, -30.1) * mm});
            skSolve(sketch);
        }
        {
            var Q0;
            Q0=makeQuery(id+"F33.imprint","IMPRINT",FACE,{"disambiguationData":[TD([[makeQuery(id+"F33.imprint","IMPRINT",EDGE,{"derivedFrom":sQuery(id+"F33.wireOp",EDGE,"E51.bottom")}),-1.0]])]});
            var Q1;
            Q1=makeQuery(id+"F33.imprint","IMPRINT",FACE,{"disambiguationData":[TD([[makeQuery(id+"F33.imprint","IMPRINT",EDGE,{"derivedFrom":sQuery(id+"F33.wireOp",EDGE,"E49.bottom")}),-1.0]])]});
            var Q2;
            Q2=makeQuery(id+"F33.imprint","IMPRINT",FACE,{"disambiguationData":[TD([[makeQuery(id+"F33.imprint","IMPRINT",EDGE,{"derivedFrom":sQuery(id+"F33.wireOp",EDGE,"E50.bottom")}),-1.0]])]});
            extrude(context, id + "F34", {"entities" : qUnion([Q0, Q1, Q2]), "operationType" : NewBodyOperationType.ADD, "depth" : 127 * mm, "offsetDistance" : 25.4 * mm});
        }
        {
            var Q0;
            Q0=makeQuery(id+"F16.boolean.opBoolean","MERGE",FACE,{"derivedFrom":[makeQuery(id+"F10.boolean.opBoolean","MERGE",FACE,{"derivedFrom":[makeQuery(id+"F1.opExtrude","CAP_FACE",FACE,{"disambiguationData":[OSD([sQuery(id+"F0.wireOp",EDGE,"E0"),sQuery(id+"F0.wireOp",EDGE,"E1"),sQuery(id+"F0.wireOp",EDGE,"E3"),sQuery(id+"F0.wireOp",EDGE,"E4"),sQuery(id+"F0.wireOp",EDGE,"E5")])],"isStart":true}),makeQuery(id+"F10.opExtrude","SWEPT_FACE",FACE,{"disambiguationData":[OSD([sQuery(id+"F9.wireOp",EDGE,"E15.right")])]})]}),makeQuery(id+"F16.opExtrude","SWEPT_FACE",FACE,{"disambiguationData":[OSD([sQuery(id+"F15.wireOp",EDGE,"E21.left")])]})]});
            var sketch = newSketch(context, id + "F35", { "sketchPlane" : qUnion([Q0])});
            skLineSegment(sketch, "E52.bottom", {"start": v(50.8, -46.99) * mm, "end": v(55.88, -46.99) * mm});
            skLineSegment(sketch, "E52.top", {"start": v(50.8, -50.8) * mm, "end": v(55.88, -50.8) * mm});
            skLineSegment(sketch, "E52.left", {"start": v(50.8, -46.99) * mm, "end": v(50.8, -50.8) * mm});
            skLineSegment(sketch, "E52.right", {"start": v(55.88, -46.99) * mm, "end": v(55.88, -50.8) * mm});
            skSolve(sketch);
        }
        {
            var Q0;
            Q0=makeQuery(id+"F35.imprint","IMPRINT",FACE,{"disambiguationData":[TD([[makeQuery(id+"F35.imprint","IMPRINT",EDGE,{"derivedFrom":sQuery(id+"F35.wireOp",EDGE,"E52.bottom")}),-1.0]])]});
            extrude(context, id + "F36", {"entities" : qUnion([Q0]), "operationType" : NewBodyOperationType.ADD, "depth" : 30.48 * mm, "offsetDistance" : 25.4 * mm});
        }
        {
            var Q0;
            {var subQ0=sQuery(id+"F2.wireOp",EDGE,"E10");Q0=makeQuery(id+"F16.boolean.opBoolean","MERGE",FACE,{"derivedFrom":[makeQuery(id+"F5.boolean.opBoolean","MERGE",FACE,{"derivedFrom":[makeQuery(id+"F4.boolean.opBoolean","MERGE",FACE,{"derivedFrom":[makeQuery(id+"F3.boolean.opBoolean","MERGE",FACE,{"derivedFrom":[makeQuery(id+"F1.opExtrude","CAP_FACE",FACE,{"disambiguationData":[OSD([sQuery(id+"F0.wireOp",EDGE,"E0"),sQuery(id+"F0.wireOp",EDGE,"E1"),sQuery(id+"F0.wireOp",EDGE,"E3"),sQuery(id+"F0.wireOp",EDGE,"E4"),sQuery(id+"F0.wireOp",EDGE,"E5")])],"isStart":false}),makeQuery(id+"F3.opExtrude","SWEPT_FACE",FACE,{"disambiguationData":[OSD([sQuery(id+"F2.wireOp",EDGE,"E9")])]})]}),makeQuery(id+"F4.opExtrude","SWEPT_FACE",FACE,{"disambiguationData":[OSD([subQ0])]})]}),makeQuery(id+"F5.opExtrude","SWEPT_FACE",FACE,{"disambiguationData":[OSD([subQ0])]})]}),makeQuery(id+"F16.opExtrude","SWEPT_FACE",FACE,{"disambiguationData":[OSD([sQuery(id+"F15.wireOp",EDGE,"E24.left")])]})]});}
            var sketch = newSketch(context, id + "F37", { "sketchPlane" : qUnion([Q0])});
            skLineSegment(sketch, "E53.bottom", {"start": v(-25.4, -50.8) * mm, "end": v(-19.05, -50.8) * mm});
            skLineSegment(sketch, "E53.top", {"start": v(-25.4, -44.96) * mm, "end": v(-19.05, -44.96) * mm});
            skLineSegment(sketch, "E53.left", {"start": v(-25.4, -50.8) * mm, "end": v(-25.4, -44.96) * mm});
            skLineSegment(sketch, "E53.right", {"start": v(-19.05, -50.8) * mm, "end": v(-19.05, -44.96) * mm});
            skLineSegment(sketch, "E54.bottom", {"start": v(-19.05, -44.96) * mm, "end": v(-12.7, -44.96) * mm});
            skLineSegment(sketch, "E54.top", {"start": v(-19.05, -39.12) * mm, "end": v(-12.7, -39.12) * mm});
            skLineSegment(sketch, "E54.left", {"start": v(-19.05, -44.96) * mm, "end": v(-19.05, -39.12) * mm});
            skLineSegment(sketch, "E54.right", {"start": v(-12.7, -44.96) * mm, "end": v(-12.7, -39.12) * mm});
            skLineSegment(sketch, "E55.bottom", {"start": v(-12.7, -39.12) * mm, "end": v(-6.35, -39.12) * mm});
            skLineSegment(sketch, "E55.top", {"start": v(-12.7, -33.27) * mm, "end": v(-6.35, -33.27) * mm});
            skLineSegment(sketch, "E55.left", {"start": v(-12.7, -39.12) * mm, "end": v(-12.7, -33.27) * mm});
            skLineSegment(sketch, "E55.right", {"start": v(-6.35, -39.12) * mm, "end": v(-6.35, -33.27) * mm});
            skLineSegment(sketch, "E56.bottom", {"start": v(-6.35, -33.27) * mm, "end": v(0, -33.27) * mm});
            skLineSegment(sketch, "E56.top", {"start": v(-6.35, -27.43) * mm, "end": v(0, -27.43) * mm});
            skLineSegment(sketch, "E56.left", {"start": v(-6.35, -33.27) * mm, "end": v(-6.35, -27.43) * mm});
            skLineSegment(sketch, "E56.right", {"start": v(0, -33.27) * mm, "end": v(0, -27.43) * mm});
            skLineSegment(sketch, "E57.bottom", {"start": v(0, -27.43) * mm, "end": v(6.35, -27.43) * mm});
            skLineSegment(sketch, "E57.top", {"start": v(0, -21.6) * mm, "end": v(6.35, -21.6) * mm});
            skLineSegment(sketch, "E57.left", {"start": v(0, -27.43) * mm, "end": v(0, -21.6) * mm});
            skLineSegment(sketch, "E57.right", {"start": v(6.35, -27.43) * mm, "end": v(6.35, -21.6) * mm});
            skLineSegment(sketch, "E58.bottom", {"start": v(6.35, -21.6) * mm, "end": v(12.7, -21.6) * mm});
            skLineSegment(sketch, "E58.top", {"start": v(6.35, -15.75) * mm, "end": v(12.7, -15.75) * mm});
            skLineSegment(sketch, "E58.left", {"start": v(6.35, -21.6) * mm, "end": v(6.35, -15.75) * mm});
            skLineSegment(sketch, "E58.right", {"start": v(12.7, -21.6) * mm, "end": v(12.7, -15.75) * mm});
            skLineSegment(sketch, "E59.bottom", {"start": v(12.7, -15.75) * mm, "end": v(19.05, -15.75) * mm});
            skLineSegment(sketch, "E59.top", {"start": v(12.7, -9.9) * mm, "end": v(19.05, -9.9) * mm});
            skLineSegment(sketch, "E59.left", {"start": v(12.7, -15.75) * mm, "end": v(12.7, -9.9) * mm});
            skLineSegment(sketch, "E59.right", {"start": v(19.05, -15.75) * mm, "end": v(19.05, -9.9) * mm});
            skLineSegment(sketch, "E60.bottom", {"start": v(19.05, -9.9) * mm, "end": v(25.4, -9.9) * mm});
            skLineSegment(sketch, "E60.top", {"start": v(19.05, -4.06) * mm, "end": v(25.4, -4.06) * mm});
            skLineSegment(sketch, "E60.left", {"start": v(19.05, -9.9) * mm, "end": v(19.05, -4.06) * mm});
            skLineSegment(sketch, "E60.right", {"start": v(25.4, -9.9) * mm, "end": v(25.4, -4.06) * mm});
            skLineSegment(sketch, "E61.bottom", {"start": v(25.4, -4.06) * mm, "end": v(31.75, -4.06) * mm});
            skLineSegment(sketch, "E61.top", {"start": v(25.4, 1.78) * mm, "end": v(31.75, 1.78) * mm});
            skLineSegment(sketch, "E61.left", {"start": v(25.4, -4.06) * mm, "end": v(25.4, 1.78) * mm});
            skLineSegment(sketch, "E61.right", {"start": v(31.75, -4.06) * mm, "end": v(31.75, 1.78) * mm});
            skLineSegment(sketch, "E62.bottom", {"start": v(31.75, 1.78) * mm, "end": v(177.8, 1.78) * mm});
            skLineSegment(sketch, "E62.top", {"start": v(31.75, -4.06) * mm, "end": v(177.8, -4.06) * mm});
            skLineSegment(sketch, "E62.left", {"start": v(31.75, 1.78) * mm, "end": v(31.75, -4.06) * mm});
            skLineSegment(sketch, "E62.right", {"start": v(177.8, 1.78) * mm, "end": v(177.8, -4.06) * mm});
            skSolve(sketch);
        }
        {
            var Q0;
            Q0=makeQuery(id+"F37.imprint","IMPRINT",FACE,{"disambiguationData":[TD([[makeQuery(id+"F37.imprint","IMPRINT",EDGE,{"derivedFrom":sQuery(id+"F37.wireOp",EDGE,"E54.bottom")}),1.0]])]});
            var Q1;
            Q1=makeQuery(id+"F37.imprint","IMPRINT",FACE,{"disambiguationData":[TD([[makeQuery(id+"F37.imprint","IMPRINT",EDGE,{"derivedFrom":sQuery(id+"F37.wireOp",EDGE,"E53.bottom")}),1.0]])]});
            var Q2;
            Q2=makeQuery(id+"F37.imprint","IMPRINT",FACE,{"disambiguationData":[TD([[makeQuery(id+"F37.imprint","IMPRINT",EDGE,{"derivedFrom":sQuery(id+"F37.wireOp",EDGE,"E55.bottom")}),1.0]])]});
            var Q3;
            Q3=makeQuery(id+"F37.imprint","IMPRINT",FACE,{"disambiguationData":[TD([[makeQuery(id+"F37.imprint","IMPRINT",EDGE,{"derivedFrom":sQuery(id+"F37.wireOp",EDGE,"E56.bottom")}),1.0]])]});
            var Q4;
            Q4=makeQuery(id+"F37.imprint","IMPRINT",FACE,{"disambiguationData":[TD([[makeQuery(id+"F37.imprint","IMPRINT",EDGE,{"derivedFrom":sQuery(id+"F37.wireOp",EDGE,"E57.bottom")}),1.0]])]});
            var Q5;
            Q5=makeQuery(id+"F37.imprint","IMPRINT",FACE,{"disambiguationData":[TD([[makeQuery(id+"F37.imprint","IMPRINT",EDGE,{"derivedFrom":sQuery(id+"F37.wireOp",EDGE,"E58.bottom")}),1.0]])]});
            var Q6;
            Q6=makeQuery(id+"F37.imprint","IMPRINT",FACE,{"disambiguationData":[TD([[makeQuery(id+"F37.imprint","IMPRINT",EDGE,{"derivedFrom":sQuery(id+"F37.wireOp",EDGE,"E59.bottom")}),1.0]])]});
            var Q7;
            Q7=makeQuery(id+"F37.imprint","IMPRINT",FACE,{"disambiguationData":[TD([[makeQuery(id+"F37.imprint","IMPRINT",EDGE,{"derivedFrom":sQuery(id+"F37.wireOp",EDGE,"E60.bottom")}),1.0]])]});
            var Q8;
            Q8=makeQuery(id+"F37.imprint","IMPRINT",FACE,{"disambiguationData":[TD([[makeQuery(id+"F37.imprint","IMPRINT",EDGE,{"derivedFrom":sQuery(id+"F37.wireOp",EDGE,"E61.bottom")}),1.0]])]});
            extrude(context, id + "F38", {"entities" : qUnion([Q0, Q1, Q2, Q3, Q4, Q5, Q6, Q7, Q8]), "depth" : 25.4 * mm, "offsetDistance" : 25.4 * mm});
        }
        {
            var Q0;
            Q0=makeQuery(id+"F37.imprint","IMPRINT",FACE,{"disambiguationData":[TD([[makeQuery(id+"F37.imprint","IMPRINT",EDGE,{"derivedFrom":sQuery(id+"F37.wireOp",EDGE,"E62.bottom")}),-1.0]])]});
            extrude(context, id + "F39", {"entities" : qUnion([Q0]), "depth" : 50.8 * mm, "offsetDistance" : 25.4 * mm});
        }
        {
            var Q0;
            Q0=makeQuery(id+"F39.opExtrude","SWEPT_FACE",FACE,{"disambiguationData":[OSD([sQuery(id+"F37.wireOp",EDGE,"E62.bottom")])]});
            var sketch = newSketch(context, id + "F40", { "sketchPlane" : qUnion([Q0])});
            skLineSegment(sketch, "E63.bottom", {"start": v(31.75, -553.72) * mm, "end": v(36.83, -553.72) * mm});
            skLineSegment(sketch, "E63.top", {"start": v(31.75, -558.8) * mm, "end": v(36.83, -558.8) * mm});
            skLineSegment(sketch, "E63.left", {"start": v(31.75, -553.72) * mm, "end": v(31.75, -558.8) * mm});
            skLineSegment(sketch, "E63.right", {"start": v(36.83, -553.72) * mm, "end": v(36.83, -558.8) * mm});
            skLineSegment(sketch, "E64.bottom", {"start": v(99.24, -553.72) * mm, "end": v(104.32, -553.72) * mm});
            skLineSegment(sketch, "E64.top", {"start": v(99.24, -558.8) * mm, "end": v(104.32, -558.8) * mm});
            skLineSegment(sketch, "E64.left", {"start": v(104.32, -553.72) * mm, "end": v(104.32, -558.8) * mm});
            skLineSegment(sketch, "E64.right", {"start": v(99.24, -553.72) * mm, "end": v(99.24, -558.8) * mm});
            skLineSegment(sketch, "E65.bottom", {"start": v(177.8, -553.72) * mm, "end": v(172.72, -553.72) * mm});
            skLineSegment(sketch, "E65.top", {"start": v(177.8, -558.8) * mm, "end": v(172.72, -558.8) * mm});
            skLineSegment(sketch, "E65.left", {"start": v(177.8, -553.72) * mm, "end": v(177.8, -558.8) * mm});
            skLineSegment(sketch, "E65.right", {"start": v(172.72, -553.72) * mm, "end": v(172.72, -558.8) * mm});
            skLineSegment(sketch, "E66.bottom", {"start": v(31.75, -533.4) * mm, "end": v(36.83, -533.4) * mm});
            skLineSegment(sketch, "E66.top", {"start": v(31.75, -538.48) * mm, "end": v(36.83, -538.48) * mm});
            skLineSegment(sketch, "E66.left", {"start": v(31.75, -533.4) * mm, "end": v(31.75, -538.48) * mm});
            skLineSegment(sketch, "E66.right", {"start": v(36.83, -533.4) * mm, "end": v(36.83, -538.48) * mm});
            skSolve(sketch);
        }
        {
            var Q0;
            Q0=makeQuery(id+"F40.imprint","IMPRINT",FACE,{"disambiguationData":[TD([[makeQuery(id+"F40.imprint","IMPRINT",EDGE,{"derivedFrom":sQuery(id+"F40.wireOp",EDGE,"E66.bottom")}),-1.0]])]});
            var Q1;
            Q1=makeQuery(id+"F40.imprint","IMPRINT",FACE,{"disambiguationData":[TD([[makeQuery(id+"F40.imprint","IMPRINT",EDGE,{"derivedFrom":sQuery(id+"F40.wireOp",EDGE,"E63.bottom")}),-1.0]])]});
            var Q2;
            Q2=makeQuery(id+"F40.imprint","IMPRINT",FACE,{"disambiguationData":[TD([[makeQuery(id+"F40.imprint","IMPRINT",EDGE,{"derivedFrom":sQuery(id+"F40.wireOp",EDGE,"E64.bottom")}),-1.0]])]});
            var Q3;
            Q3=makeQuery(id+"F40.imprint","IMPRINT",FACE,{"disambiguationData":[TD([[makeQuery(id+"F40.imprint","IMPRINT",EDGE,{"derivedFrom":sQuery(id+"F40.wireOp",EDGE,"E65.bottom")}),1.0]])]});
            extrude(context, id + "F41", {"entities" : qUnion([Q0, Q1, Q2, Q3]), "operationType" : NewBodyOperationType.ADD, "depth" : 15.24 * mm, "offsetDistance" : 25.4 * mm});
        }
        {
            var Q0;
            Q0=makeQuery(id+"F41.opExtrude","SWEPT_FACE",FACE,{"disambiguationData":[OSD([sQuery(id+"F40.wireOp",EDGE,"E63.right")])]});
            var sketch = newSketch(context, id + "F42", { "sketchPlane" : qUnion([Q0])});
            skLineSegment(sketch, "E67.bottom", {"start": v(-557.02, 14.48) * mm, "end": v(-555.24, 14.48) * mm});
            skLineSegment(sketch, "E67.top", {"start": v(-557.02, 12.7) * mm, "end": v(-555.24, 12.7) * mm});
            skLineSegment(sketch, "E67.left", {"start": v(-557.02, 14.48) * mm, "end": v(-557.02, 12.7) * mm});
            skLineSegment(sketch, "E67.right", {"start": v(-555.24, 14.48) * mm, "end": v(-555.24, 12.7) * mm});
            skLineSegment(sketch, "E68.bottom", {"start": v(-557.02, 9.75) * mm, "end": v(-555.24, 9.75) * mm});
            skLineSegment(sketch, "E68.top", {"start": v(-557.02, 7.97) * mm, "end": v(-555.24, 7.97) * mm});
            skLineSegment(sketch, "E68.left", {"start": v(-557.02, 9.75) * mm, "end": v(-557.02, 7.97) * mm});
            skLineSegment(sketch, "E68.right", {"start": v(-555.24, 9.75) * mm, "end": v(-555.24, 7.97) * mm});
            skLineSegment(sketch, "E69.bottom", {"start": v(-557.02, 5.32) * mm, "end": v(-555.24, 5.32) * mm});
            skLineSegment(sketch, "E69.top", {"start": v(-557.02, 3.55) * mm, "end": v(-555.24, 3.55) * mm});
            skLineSegment(sketch, "E69.left", {"start": v(-557.02, 5.32) * mm, "end": v(-557.02, 3.55) * mm});
            skLineSegment(sketch, "E69.right", {"start": v(-555.24, 5.32) * mm, "end": v(-555.24, 3.55) * mm});
            skSolve(sketch);
        }
        {
            var Q0;
            Q0=makeQuery(id+"F42.imprint","IMPRINT",FACE,{"disambiguationData":[TD([[makeQuery(id+"F42.imprint","IMPRINT",EDGE,{"derivedFrom":sQuery(id+"F42.wireOp",EDGE,"E67.bottom")}),-1.0]])]});
            var Q1;
            Q1=makeQuery(id+"F42.imprint","IMPRINT",FACE,{"disambiguationData":[TD([[makeQuery(id+"F42.imprint","IMPRINT",EDGE,{"derivedFrom":sQuery(id+"F42.wireOp",EDGE,"E68.bottom")}),-1.0]])]});
            var Q2;
            Q2=makeQuery(id+"F42.imprint","IMPRINT",FACE,{"disambiguationData":[TD([[makeQuery(id+"F42.imprint","IMPRINT",EDGE,{"derivedFrom":sQuery(id+"F42.wireOp",EDGE,"E69.bottom")}),-1.0]])]});
            extrude(context, id + "F43", {"entities" : qUnion([Q0, Q1, Q2]), "operationType" : NewBodyOperationType.ADD, "depth" : 139.7 * mm, "offsetDistance" : 25.4 * mm});
        }
        {
            var Q0;
            Q0=makeQuery(id+"F41.opExtrude","SWEPT_FACE",FACE,{"disambiguationData":[OSD([sQuery(id+"F40.wireOp",EDGE,"E65.bottom")])]});
            var sketch = newSketch(context, id + "F44", { "sketchPlane" : qUnion([Q0])});
            skLineSegment(sketch, "E70.bottom", {"start": v(-176.02, 14.85) * mm, "end": v(-174.24, 14.85) * mm});
            skLineSegment(sketch, "E70.top", {"start": v(-176.02, 13.07) * mm, "end": v(-174.24, 13.07) * mm});
            skLineSegment(sketch, "E70.left", {"start": v(-176.02, 14.85) * mm, "end": v(-176.02, 13.07) * mm});
            skLineSegment(sketch, "E70.right", {"start": v(-174.24, 14.85) * mm, "end": v(-174.24, 13.07) * mm});
            skLineSegment(sketch, "E71.bottom", {"start": v(-176.02, 10.61) * mm, "end": v(-174.24, 10.61) * mm});
            skLineSegment(sketch, "E71.top", {"start": v(-176.02, 8.84) * mm, "end": v(-174.24, 8.84) * mm});
            skLineSegment(sketch, "E71.left", {"start": v(-176.02, 10.61) * mm, "end": v(-176.02, 8.84) * mm});
            skLineSegment(sketch, "E71.right", {"start": v(-174.24, 10.61) * mm, "end": v(-174.24, 8.84) * mm});
            skLineSegment(sketch, "E72.bottom", {"start": v(-176.02, 5.58) * mm, "end": v(-174.24, 5.58) * mm});
            skLineSegment(sketch, "E72.top", {"start": v(-176.02, 3.8) * mm, "end": v(-174.24, 3.8) * mm});
            skLineSegment(sketch, "E72.left", {"start": v(-176.02, 5.58) * mm, "end": v(-176.02, 3.8) * mm});
            skLineSegment(sketch, "E72.right", {"start": v(-174.24, 5.58) * mm, "end": v(-174.24, 3.8) * mm});
            skSolve(sketch);
        }
        {
            var Q0;
            Q0=makeQuery(id+"F44.imprint","IMPRINT",FACE,{"disambiguationData":[TD([[makeQuery(id+"F44.imprint","IMPRINT",EDGE,{"derivedFrom":sQuery(id+"F44.wireOp",EDGE,"E70.bottom")}),-1.0]])]});
            var Q1;
            Q1=makeQuery(id+"F44.imprint","IMPRINT",FACE,{"disambiguationData":[TD([[makeQuery(id+"F44.imprint","IMPRINT",EDGE,{"derivedFrom":sQuery(id+"F44.wireOp",EDGE,"E71.bottom")}),-1.0]])]});
            var Q2;
            Q2=makeQuery(id+"F44.imprint","IMPRINT",FACE,{"disambiguationData":[TD([[makeQuery(id+"F44.imprint","IMPRINT",EDGE,{"derivedFrom":sQuery(id+"F44.wireOp",EDGE,"E72.bottom")}),-1.0]])]});
            extrude(context, id + "F45", {"entities" : qUnion([Q0, Q1, Q2]), "depth" : 50.8 * mm, "offsetDistance" : 25.4 * mm});
        }
        {
            var Q0;
            Q0=makeQuery(id+"F41.opExtrude","SWEPT_FACE",FACE,{"disambiguationData":[OSD([sQuery(id+"F40.wireOp",EDGE,"E66.top")])]});
            var sketch = newSketch(context, id + "F46", { "sketchPlane" : qUnion([Q0])});
            skLineSegment(sketch, "E73.bottom", {"start": v(33.53, 14.48) * mm, "end": v(35.3, 14.48) * mm});
            skLineSegment(sketch, "E73.top", {"start": v(33.53, 12.7) * mm, "end": v(35.3, 12.7) * mm});
            skLineSegment(sketch, "E73.left", {"start": v(33.53, 14.48) * mm, "end": v(33.53, 12.7) * mm});
            skLineSegment(sketch, "E73.right", {"start": v(35.3, 14.48) * mm, "end": v(35.3, 12.7) * mm});
            skLineSegment(sketch, "E74.bottom", {"start": v(33.53, 10.16) * mm, "end": v(35.3, 10.16) * mm});
            skLineSegment(sketch, "E74.top", {"start": v(33.53, 8.38) * mm, "end": v(35.3, 8.38) * mm});
            skLineSegment(sketch, "E74.left", {"start": v(33.53, 10.16) * mm, "end": v(33.53, 8.38) * mm});
            skLineSegment(sketch, "E74.right", {"start": v(35.3, 10.16) * mm, "end": v(35.3, 8.38) * mm});
            skLineSegment(sketch, "E75.bottom", {"start": v(33.53, 6.1) * mm, "end": v(35.3, 6.1) * mm});
            skLineSegment(sketch, "E75.top", {"start": v(33.53, 4.32) * mm, "end": v(35.3, 4.32) * mm});
            skLineSegment(sketch, "E75.left", {"start": v(33.53, 6.1) * mm, "end": v(33.53, 4.32) * mm});
            skLineSegment(sketch, "E75.right", {"start": v(35.3, 6.1) * mm, "end": v(35.3, 4.32) * mm});
            skSolve(sketch);
        }
        {
            var Q0;
            Q0=makeQuery(id+"F46.imprint","IMPRINT",FACE,{"disambiguationData":[TD([[makeQuery(id+"F46.imprint","IMPRINT",EDGE,{"derivedFrom":sQuery(id+"F46.wireOp",EDGE,"E73.bottom")}),-1.0]])]});
            var Q1;
            Q1=makeQuery(id+"F46.imprint","IMPRINT",FACE,{"disambiguationData":[TD([[makeQuery(id+"F46.imprint","IMPRINT",EDGE,{"derivedFrom":sQuery(id+"F46.wireOp",EDGE,"E74.bottom")}),-1.0]])]});
            var Q2;
            Q2=makeQuery(id+"F46.imprint","IMPRINT",FACE,{"disambiguationData":[TD([[makeQuery(id+"F46.imprint","IMPRINT",EDGE,{"derivedFrom":sQuery(id+"F46.wireOp",EDGE,"E75.bottom")}),-1.0]])]});
            extrude(context, id + "F47", {"entities" : qUnion([Q0, Q1, Q2]), "operationType" : NewBodyOperationType.ADD, "depth" : 17.78 * mm, "offsetDistance" : 25.4 * mm});
        }
        {
            var Q0;
            Q0=makeQuery(id+"F24.boolean.opBoolean","MERGE",FACE,{"derivedFrom":[makeQuery(id+"F1.opExtrude","SWEPT_FACE",FACE,{"disambiguationData":[OSD([sQuery(id+"F0.wireOp",EDGE,"E3")])]}),makeQuery(id+"F24.opExtrude","CAP_FACE",FACE,{"disambiguationData":[OSD([sQuery(id+"F23.wireOp",EDGE,"E30"),sQuery(id+"F23.wireOp",EDGE,"E31"),sQuery(id+"F23.wireOp",EDGE,"E32")])],"isStart":true}),makeQuery(id+"F24.opExtrude","CAP_FACE",FACE,{"disambiguationData":[OSD([sQuery(id+"F23.wireOp",EDGE,"E33"),sQuery(id+"F23.wireOp",EDGE,"E34"),sQuery(id+"F23.wireOp",EDGE,"E35")])],"isStart":true})]});
            var sketch = newSketch(context, id + "F48", { "sketchPlane" : qUnion([Q0])});
            skLineSegment(sketch, "E76.bottom", {"start": v(88.9, -46.99) * mm, "end": v(419.1, -46.99) * mm});
            skLineSegment(sketch, "E76.top", {"start": v(88.9, -50.8) * mm, "end": v(419.1, -50.8) * mm});
            skLineSegment(sketch, "E76.left", {"start": v(88.9, -46.99) * mm, "end": v(88.9, -50.8) * mm});
            skLineSegment(sketch, "E76.right", {"start": v(419.1, -46.99) * mm, "end": v(419.1, -50.8) * mm});
            skSolve(sketch);
        }
        {
            var Q0;
            Q0=makeQuery(id+"F48.imprint","IMPRINT",FACE,{"disambiguationData":[TD([[makeQuery(id+"F48.imprint","IMPRINT",EDGE,{"derivedFrom":sQuery(id+"F48.wireOp",EDGE,"E76.bottom")}),-1.0]])]});
            extrude(context, id + "F49", {"entities" : qUnion([Q0]), "operationType" : NewBodyOperationType.ADD, "depth" : 38.1 * mm, "offsetDistance" : 25.4 * mm});
        }
        {
            var Q0;
            Q0=makeQuery(id+"F16.opExtrude","SWEPT_FACE",FACE,{"disambiguationData":[OSD([sQuery(id+"F15.wireOp",EDGE,"E21.right")])]});
            var sketch = newSketch(context, id + "F50", { "sketchPlane" : qUnion([Q0])});
            skLineSegment(sketch, "E77.bottom", {"start": v(-88.9, -46.99) * mm, "end": v(-190.5, -46.99) * mm});
            skLineSegment(sketch, "E77.top", {"start": v(-88.9, -50.8) * mm, "end": v(-190.5, -50.8) * mm});
            skLineSegment(sketch, "E77.left", {"start": v(-88.9, -46.99) * mm, "end": v(-88.9, -50.8) * mm});
            skLineSegment(sketch, "E77.right", {"start": v(-190.5, -46.99) * mm, "end": v(-190.5, -50.8) * mm});
            skSolve(sketch);
        }
        {
            var Q0;
            Q0=makeQuery(id+"F50.imprint","IMPRINT",FACE,{"disambiguationData":[TD([[makeQuery(id+"F50.imprint","IMPRINT",EDGE,{"derivedFrom":sQuery(id+"F50.wireOp",EDGE,"E77.bottom")}),1.0]])]});
            extrude(context, id + "F51", {"entities" : qUnion([Q0]), "operationType" : NewBodyOperationType.ADD, "depth" : 38.1 * mm, "offsetDistance" : 25.4 * mm});
        }
        {
            var Q0;
            Q0=makeQuery(id+"F16.opExtrude","SWEPT_FACE",FACE,{"disambiguationData":[OSD([sQuery(id+"F15.wireOp",EDGE,"E24.right")])]});
            var sketch = newSketch(context, id + "F52", { "sketchPlane" : qUnion([Q0])});
            skLineSegment(sketch, "E78.bottom", {"start": v(88.9, -47) * mm, "end": v(190.5, -47) * mm});
            skLineSegment(sketch, "E78.top", {"start": v(88.9, -50.8) * mm, "end": v(190.5, -50.8) * mm});
            skLineSegment(sketch, "E78.left", {"start": v(88.9, -47) * mm, "end": v(88.9, -50.8) * mm});
            skLineSegment(sketch, "E78.right", {"start": v(190.5, -47) * mm, "end": v(190.5, -50.8) * mm});
            skSolve(sketch);
        }
        {
            var Q0;
            Q0=makeQuery(id+"F52.imprint","IMPRINT",FACE,{"disambiguationData":[TD([[makeQuery(id+"F52.imprint","IMPRINT",EDGE,{"derivedFrom":sQuery(id+"F52.wireOp",EDGE,"E78.bottom")}),-1.0]])]});
            extrude(context, id + "F53", {"entities" : qUnion([Q0]), "operationType" : NewBodyOperationType.ADD, "depth" : 38.1 * mm, "offsetDistance" : 25.4 * mm});
        }
        {
            var Q0;
            Q0=makeQuery(id+"F49.opExtrude","CAP_FACE",FACE,{"disambiguationData":[OSD([sQuery(id+"F48.wireOp",EDGE,"E76.bottom"),sQuery(id+"F48.wireOp",EDGE,"E76.top"),sQuery(id+"F48.wireOp",EDGE,"E76.left"),sQuery(id+"F48.wireOp",EDGE,"E76.right")])],"isStart":false});
            var sketch = newSketch(context, id + "F54", { "sketchPlane" : qUnion([Q0])});
            skLineSegment(sketch, "E79.bottom", {"start": v(238.85, -50.8) * mm, "end": v(254.1, -50.8) * mm});
            skLineSegment(sketch, "E79.top", {"start": v(238.85, -48.26) * mm, "end": v(254.1, -48.26) * mm});
            skLineSegment(sketch, "E79.left", {"start": v(238.85, -50.8) * mm, "end": v(238.85, -48.26) * mm});
            skLineSegment(sketch, "E79.right", {"start": v(254.1, -50.8) * mm, "end": v(254.1, -48.26) * mm});
            skSolve(sketch);
        }
        {
            var Q0;
            Q0=makeQuery(id+"F54.imprint","IMPRINT",FACE,{"disambiguationData":[TD([[makeQuery(id+"F54.imprint","IMPRINT",EDGE,{"derivedFrom":sQuery(id+"F54.wireOp",EDGE,"E79.bottom")}),-1.0]])]});
            extrude(context, id + "F55", {"entities" : qUnion([Q0]), "operationType" : NewBodyOperationType.ADD, "depth" : 2.54 * mm, "offsetDistance" : 25.4 * mm});
        }
        {
            var Q0;
            Q0=makeQuery(id+"F53.boolean.opBoolean","MERGE",FACE,{"derivedFrom":[makeQuery(id+"F51.boolean.opBoolean","MERGE",FACE,{"derivedFrom":[makeQuery(id+"F49.opExtrude","SWEPT_FACE",FACE,{"disambiguationData":[OSD([sQuery(id+"F48.wireOp",EDGE,"E76.bottom")])]}),makeQuery(id+"F51.opExtrude","SWEPT_FACE",FACE,{"disambiguationData":[OSD([sQuery(id+"F50.wireOp",EDGE,"E77.bottom")])]})]}),makeQuery(id+"F53.opExtrude","SWEPT_FACE",FACE,{"disambiguationData":[OSD([sQuery(id+"F52.wireOp",EDGE,"E78.bottom")])]})]});
            var sketch = newSketch(context, id + "F56", { "sketchPlane" : qUnion([Q0])});
            skLineSegment(sketch, "E80.bottom", {"start": v(-85.85, -235.83) * mm, "end": v(-88.9, -235.83) * mm});
            skLineSegment(sketch, "E80.top", {"start": v(-85.85, -238.88) * mm, "end": v(-88.9, -238.88) * mm});
            skLineSegment(sketch, "E80.left", {"start": v(-85.85, -235.83) * mm, "end": v(-85.85, -238.88) * mm});
            skLineSegment(sketch, "E80.right", {"start": v(-88.9, -235.83) * mm, "end": v(-88.9, -238.88) * mm});
            skLineSegment(sketch, "E81.bottom", {"start": v(-85.85, -254) * mm, "end": v(-88.9, -254) * mm});
            skLineSegment(sketch, "E81.top", {"start": v(-85.85, -257.05) * mm, "end": v(-88.9, -257.05) * mm});
            skLineSegment(sketch, "E81.left", {"start": v(-85.85, -254) * mm, "end": v(-85.85, -257.05) * mm});
            skLineSegment(sketch, "E81.right", {"start": v(-88.9, -254) * mm, "end": v(-88.9, -257.05) * mm});
            skLineSegment(sketch, "E82.bottom", {"start": v(-187.45, -381) * mm, "end": v(-190.5, -381) * mm});
            skLineSegment(sketch, "E82.top", {"start": v(-187.45, -384.05) * mm, "end": v(-190.5, -384.05) * mm});
            skLineSegment(sketch, "E82.left", {"start": v(-187.45, -381) * mm, "end": v(-187.45, -384.05) * mm});
            skLineSegment(sketch, "E82.right", {"start": v(-190.5, -381) * mm, "end": v(-190.5, -384.05) * mm});
            skLineSegment(sketch, "E83.bottom", {"start": v(-190.5, -123.95) * mm, "end": v(-187.45, -123.95) * mm});
            skLineSegment(sketch, "E83.top", {"start": v(-190.5, -127) * mm, "end": v(-187.45, -127) * mm});
            skLineSegment(sketch, "E83.left", {"start": v(-190.5, -123.95) * mm, "end": v(-190.5, -127) * mm});
            skLineSegment(sketch, "E83.right", {"start": v(-187.45, -123.95) * mm, "end": v(-187.45, -127) * mm});
            skLineSegment(sketch, "E84.bottom", {"start": v(-88.9, -127) * mm, "end": v(-85.85, -127) * mm});
            skLineSegment(sketch, "E84.top", {"start": v(-88.9, -123.95) * mm, "end": v(-85.85, -123.95) * mm});
            skLineSegment(sketch, "E84.left", {"start": v(-88.9, -127) * mm, "end": v(-88.9, -123.95) * mm});
            skLineSegment(sketch, "E84.right", {"start": v(-85.85, -127) * mm, "end": v(-85.85, -123.95) * mm});
            skLineSegment(sketch, "E85.bottom", {"start": v(-88.9, -381) * mm, "end": v(-85.85, -381) * mm});
            skLineSegment(sketch, "E85.top", {"start": v(-88.9, -384.05) * mm, "end": v(-85.85, -384.05) * mm});
            skLineSegment(sketch, "E85.left", {"start": v(-88.9, -381) * mm, "end": v(-88.9, -384.05) * mm});
            skLineSegment(sketch, "E85.right", {"start": v(-85.85, -381) * mm, "end": v(-85.85, -384.05) * mm});
            skSolve(sketch);
        }
        {
            var Q0;
            Q0=makeQuery(id+"F56.imprint","IMPRINT",FACE,{"disambiguationData":[TD([[makeQuery(id+"F56.imprint","IMPRINT",EDGE,{"derivedFrom":sQuery(id+"F56.wireOp",EDGE,"E83.bottom")}),-1.0]])]});
            var Q1;
            Q1=makeQuery(id+"F56.imprint","IMPRINT",FACE,{"disambiguationData":[TD([[makeQuery(id+"F56.imprint","IMPRINT",EDGE,{"derivedFrom":sQuery(id+"F56.wireOp",EDGE,"E84.bottom")}),1.0]])]});
            var Q2;
            Q2=makeQuery(id+"F56.imprint","IMPRINT",FACE,{"disambiguationData":[TD([[makeQuery(id+"F56.imprint","IMPRINT",EDGE,{"derivedFrom":sQuery(id+"F56.wireOp",EDGE,"E80.bottom")}),1.0]])]});
            var Q3;
            Q3=makeQuery(id+"F56.imprint","IMPRINT",FACE,{"disambiguationData":[TD([[makeQuery(id+"F56.imprint","IMPRINT",EDGE,{"derivedFrom":sQuery(id+"F56.wireOp",EDGE,"E81.bottom")}),1.0]])]});
            var Q4;
            Q4=makeQuery(id+"F56.imprint","IMPRINT",FACE,{"disambiguationData":[TD([[makeQuery(id+"F56.imprint","IMPRINT",EDGE,{"derivedFrom":sQuery(id+"F56.wireOp",EDGE,"E85.bottom")}),-1.0]])]});
            var Q5;
            Q5=makeQuery(id+"F56.imprint","IMPRINT",FACE,{"disambiguationData":[TD([[makeQuery(id+"F56.imprint","IMPRINT",EDGE,{"derivedFrom":sQuery(id+"F56.wireOp",EDGE,"E82.bottom")}),1.0]])]});
            extrude(context, id + "F57", {"entities" : qUnion([Q0, Q1, Q2, Q3, Q4, Q5]), "operationType" : NewBodyOperationType.ADD, "depth" : 12.7 * mm, "offsetDistance" : 25.4 * mm});
        }
        {
            var Q0;
            Q0=makeQuery(id+"F57.opExtrude","SWEPT_FACE",FACE,{"disambiguationData":[OSD([sQuery(id+"F56.wireOp",EDGE,"E83.right")])]});
            var sketch = newSketch(context, id + "F58", { "sketchPlane" : qUnion([Q0])});
            skLineSegment(sketch, "E86.bottom", {"start": v(-125.98, -35.56) * mm, "end": v(-124.71, -35.56) * mm});
            skLineSegment(sketch, "E86.top", {"start": v(-125.98, -36.83) * mm, "end": v(-124.71, -36.83) * mm});
            skLineSegment(sketch, "E86.left", {"start": v(-125.98, -35.56) * mm, "end": v(-125.98, -36.83) * mm});
            skLineSegment(sketch, "E86.right", {"start": v(-124.71, -35.56) * mm, "end": v(-124.71, -36.83) * mm});
            skLineSegment(sketch, "E87.bottom", {"start": v(-125.98, -39.37) * mm, "end": v(-124.71, -39.37) * mm});
            skLineSegment(sketch, "E87.top", {"start": v(-125.98, -40.64) * mm, "end": v(-124.71, -40.64) * mm});
            skLineSegment(sketch, "E87.left", {"start": v(-125.98, -39.37) * mm, "end": v(-125.98, -40.64) * mm});
            skLineSegment(sketch, "E87.right", {"start": v(-124.71, -39.37) * mm, "end": v(-124.71, -40.64) * mm});
            skLineSegment(sketch, "E88.bottom", {"start": v(-125.98, -43.18) * mm, "end": v(-124.71, -43.18) * mm});
            skLineSegment(sketch, "E88.top", {"start": v(-125.98, -44.45) * mm, "end": v(-124.71, -44.45) * mm});
            skLineSegment(sketch, "E88.left", {"start": v(-125.98, -43.18) * mm, "end": v(-125.98, -44.45) * mm});
            skLineSegment(sketch, "E88.right", {"start": v(-124.71, -43.18) * mm, "end": v(-124.71, -44.45) * mm});
            skSolve(sketch);
        }
        {
            var Q0;
            Q0=makeQuery(id+"F57.opExtrude","SWEPT_FACE",FACE,{"disambiguationData":[OSD([sQuery(id+"F56.wireOp",EDGE,"E84.bottom")])]});
            var sketch = newSketch(context, id + "F59", { "sketchPlane" : qUnion([Q0])});
            skLineSegment(sketch, "E89.bottom", {"start": v(-87.88, -35.56) * mm, "end": v(-86.61, -35.56) * mm});
            skLineSegment(sketch, "E89.top", {"start": v(-87.88, -36.83) * mm, "end": v(-86.61, -36.83) * mm});
            skLineSegment(sketch, "E89.left", {"start": v(-87.88, -35.56) * mm, "end": v(-87.88, -36.83) * mm});
            skLineSegment(sketch, "E89.right", {"start": v(-86.61, -35.56) * mm, "end": v(-86.61, -36.83) * mm});
            skLineSegment(sketch, "E90.bottom", {"start": v(-87.88, -39.37) * mm, "end": v(-86.61, -39.37) * mm});
            skLineSegment(sketch, "E90.top", {"start": v(-87.88, -40.64) * mm, "end": v(-86.61, -40.64) * mm});
            skLineSegment(sketch, "E90.left", {"start": v(-87.88, -39.37) * mm, "end": v(-87.88, -40.64) * mm});
            skLineSegment(sketch, "E90.right", {"start": v(-86.61, -39.37) * mm, "end": v(-86.61, -40.64) * mm});
            skLineSegment(sketch, "E91.bottom", {"start": v(-87.88, -43.18) * mm, "end": v(-86.61, -43.18) * mm});
            skLineSegment(sketch, "E91.top", {"start": v(-87.88, -44.45) * mm, "end": v(-86.61, -44.45) * mm});
            skLineSegment(sketch, "E91.left", {"start": v(-87.88, -43.18) * mm, "end": v(-87.88, -44.45) * mm});
            skLineSegment(sketch, "E91.right", {"start": v(-86.61, -43.18) * mm, "end": v(-86.61, -44.45) * mm});
            skSolve(sketch);
        }
        {
            var Q0;
            Q0=makeQuery(id+"F57.opExtrude","SWEPT_FACE",FACE,{"disambiguationData":[OSD([sQuery(id+"F56.wireOp",EDGE,"E81.top")])]});
            var sketch = newSketch(context, id + "F60", { "sketchPlane" : qUnion([Q0])});
            skLineSegment(sketch, "E92.bottom", {"start": v(-87.88, -35.56) * mm, "end": v(-86.61, -35.56) * mm});
            skLineSegment(sketch, "E92.top", {"start": v(-87.88, -36.83) * mm, "end": v(-86.61, -36.83) * mm});
            skLineSegment(sketch, "E92.left", {"start": v(-87.88, -35.56) * mm, "end": v(-87.88, -36.83) * mm});
            skLineSegment(sketch, "E92.right", {"start": v(-86.61, -35.56) * mm, "end": v(-86.61, -36.83) * mm});
            skLineSegment(sketch, "E93.bottom", {"start": v(-87.88, -39.37) * mm, "end": v(-86.61, -39.37) * mm});
            skLineSegment(sketch, "E93.top", {"start": v(-87.88, -40.64) * mm, "end": v(-86.61, -40.64) * mm});
            skLineSegment(sketch, "E93.left", {"start": v(-87.88, -39.37) * mm, "end": v(-87.88, -40.64) * mm});
            skLineSegment(sketch, "E93.right", {"start": v(-86.61, -39.37) * mm, "end": v(-86.61, -40.64) * mm});
            skLineSegment(sketch, "E94.bottom", {"start": v(-87.88, -43.18) * mm, "end": v(-86.61, -43.18) * mm});
            skLineSegment(sketch, "E94.top", {"start": v(-87.88, -44.45) * mm, "end": v(-86.61, -44.45) * mm});
            skLineSegment(sketch, "E94.left", {"start": v(-87.88, -43.18) * mm, "end": v(-87.88, -44.45) * mm});
            skLineSegment(sketch, "E94.right", {"start": v(-86.61, -43.18) * mm, "end": v(-86.61, -44.45) * mm});
            skSolve(sketch);
        }
        {
            var Q0;
            Q0=makeQuery(id+"F57.opExtrude","SWEPT_FACE",FACE,{"disambiguationData":[OSD([sQuery(id+"F56.wireOp",EDGE,"E85.left")])]});
            var sketch = newSketch(context, id + "F61", { "sketchPlane" : qUnion([Q0])});
            skLineSegment(sketch, "E95.bottom", {"start": v(382.02, -35.56) * mm, "end": v(383.29, -35.56) * mm});
            skLineSegment(sketch, "E95.top", {"start": v(382.02, -36.83) * mm, "end": v(383.29, -36.83) * mm});
            skLineSegment(sketch, "E95.left", {"start": v(382.02, -35.56) * mm, "end": v(382.02, -36.83) * mm});
            skLineSegment(sketch, "E95.right", {"start": v(383.29, -35.56) * mm, "end": v(383.29, -36.83) * mm});
            skLineSegment(sketch, "E96.bottom", {"start": v(382.06, -39.37) * mm, "end": v(383.33, -39.37) * mm});
            skLineSegment(sketch, "E96.top", {"start": v(382.06, -40.64) * mm, "end": v(383.33, -40.64) * mm});
            skLineSegment(sketch, "E96.left", {"start": v(382.06, -39.37) * mm, "end": v(382.06, -40.64) * mm});
            skLineSegment(sketch, "E96.right", {"start": v(383.33, -39.37) * mm, "end": v(383.33, -40.64) * mm});
            skLineSegment(sketch, "E97.bottom", {"start": v(382.02, -43.18) * mm, "end": v(383.29, -43.18) * mm});
            skLineSegment(sketch, "E97.top", {"start": v(382.02, -44.45) * mm, "end": v(383.29, -44.45) * mm});
            skLineSegment(sketch, "E97.left", {"start": v(382.02, -43.18) * mm, "end": v(382.02, -44.45) * mm});
            skLineSegment(sketch, "E97.right", {"start": v(383.29, -43.18) * mm, "end": v(383.29, -44.45) * mm});
            skSolve(sketch);
        }
        {
            var Q0;
            Q0=makeQuery(id+"F58.imprint","IMPRINT",FACE,{"disambiguationData":[TD([[makeQuery(id+"F58.imprint","IMPRINT",EDGE,{"derivedFrom":sQuery(id+"F58.wireOp",EDGE,"E86.bottom")}),-1.0]])]});
            var Q1;
            Q1=makeQuery(id+"F58.imprint","IMPRINT",FACE,{"disambiguationData":[TD([[makeQuery(id+"F58.imprint","IMPRINT",EDGE,{"derivedFrom":sQuery(id+"F58.wireOp",EDGE,"E87.bottom")}),-1.0]])]});
            var Q2;
            Q2=makeQuery(id+"F58.imprint","IMPRINT",FACE,{"disambiguationData":[TD([[makeQuery(id+"F58.imprint","IMPRINT",EDGE,{"derivedFrom":sQuery(id+"F58.wireOp",EDGE,"E88.bottom")}),-1.0]])]});
            extrude(context, id + "F62", {"entities" : qUnion([Q0, Q1, Q2]), "operationType" : NewBodyOperationType.ADD, "depth" : 101.6 * mm, "offsetDistance" : 25.4 * mm});
        }
        {
            var Q0;
            Q0=makeQuery(id+"F59.imprint","IMPRINT",FACE,{"disambiguationData":[TD([[makeQuery(id+"F59.imprint","IMPRINT",EDGE,{"derivedFrom":sQuery(id+"F59.wireOp",EDGE,"E89.bottom")}),-1.0]])]});
            var Q1;
            Q1=makeQuery(id+"F59.imprint","IMPRINT",FACE,{"disambiguationData":[TD([[makeQuery(id+"F59.imprint","IMPRINT",EDGE,{"derivedFrom":sQuery(id+"F59.wireOp",EDGE,"E90.bottom")}),-1.0]])]});
            var Q2;
            Q2=makeQuery(id+"F59.imprint","IMPRINT",FACE,{"disambiguationData":[TD([[makeQuery(id+"F59.imprint","IMPRINT",EDGE,{"derivedFrom":sQuery(id+"F59.wireOp",EDGE,"E91.bottom")}),-1.0]])]});
            extrude(context, id + "F63", {"entities" : qUnion([Q0, Q1, Q2]), "operationType" : NewBodyOperationType.ADD, "depth" : 109.22 * mm, "offsetDistance" : 25.4 * mm});
        }
        {
            var Q0;
            Q0=makeQuery(id+"F60.imprint","IMPRINT",FACE,{"disambiguationData":[TD([[makeQuery(id+"F60.imprint","IMPRINT",EDGE,{"derivedFrom":sQuery(id+"F60.wireOp",EDGE,"E92.bottom")}),-1.0]])]});
            var Q1;
            Q1=makeQuery(id+"F60.imprint","IMPRINT",FACE,{"disambiguationData":[TD([[makeQuery(id+"F60.imprint","IMPRINT",EDGE,{"derivedFrom":sQuery(id+"F60.wireOp",EDGE,"E93.bottom")}),-1.0]])]});
            var Q2;
            Q2=makeQuery(id+"F60.imprint","IMPRINT",FACE,{"disambiguationData":[TD([[makeQuery(id+"F60.imprint","IMPRINT",EDGE,{"derivedFrom":sQuery(id+"F60.wireOp",EDGE,"E94.bottom")}),-1.0]])]});
            extrude(context, id + "F64", {"entities" : qUnion([Q0, Q1, Q2]), "operationType" : NewBodyOperationType.ADD, "depth" : 127 * mm, "offsetDistance" : 25.4 * mm});
        }
        {
            var Q0;
            Q0=makeQuery(id+"F61.imprint","IMPRINT",FACE,{"disambiguationData":[TD([[makeQuery(id+"F61.imprint","IMPRINT",EDGE,{"derivedFrom":sQuery(id+"F61.wireOp",EDGE,"E95.bottom")}),-1.0]])]});
            var Q1;
            Q1=makeQuery(id+"F61.imprint","IMPRINT",FACE,{"disambiguationData":[TD([[makeQuery(id+"F61.imprint","IMPRINT",EDGE,{"derivedFrom":sQuery(id+"F61.wireOp",EDGE,"E96.bottom")}),-1.0]])]});
            var Q2;
            Q2=makeQuery(id+"F61.imprint","IMPRINT",FACE,{"disambiguationData":[TD([[makeQuery(id+"F61.imprint","IMPRINT",EDGE,{"derivedFrom":sQuery(id+"F61.wireOp",EDGE,"E97.bottom")}),-1.0]])]});
            extrude(context, id + "F65", {"entities" : qUnion([Q0, Q1, Q2]), "operationType" : NewBodyOperationType.ADD, "depth" : 101.6 * mm, "offsetDistance" : 25.4 * mm});
        }
        {
            var Q0;
            Q0=makeQuery(id+"F55.boolean.opBoolean","MERGE",FACE,{"derivedFrom":[makeQuery(id+"F53.boolean.opBoolean","MERGE",FACE,{"derivedFrom":[makeQuery(id+"F51.boolean.opBoolean","MERGE",FACE,{"derivedFrom":[makeQuery(id+"F49.boolean.opBoolean","MERGE",FACE,{"derivedFrom":[makeQuery(id+"F36.boolean.opBoolean","MERGE",FACE,{"derivedFrom":[makeQuery(id+"F28.boolean.opBoolean","MERGE",FACE,{"derivedFrom":[makeQuery(id+"F20.boolean.opBoolean","MERGE",FACE,{"derivedFrom":[makeQuery(id+"F16.boolean.opBoolean","MERGE",FACE,{"derivedFrom":[makeQuery(id+"F13.boolean.opBoolean","MERGE",FACE,{"derivedFrom":[makeQuery(id+"F10.boolean.opBoolean","MERGE",FACE,{"derivedFrom":[makeQuery(id+"F7.boolean.opBoolean","MERGE",FACE,{"derivedFrom":[makeQuery(id+"F3.boolean.opBoolean","MERGE",FACE,{"derivedFrom":[makeQuery(id+"F1.opExtrude","SWEPT_FACE",FACE,{"disambiguationData":[OSD([sQuery(id+"F0.wireOp",EDGE,"E0")])]}),makeQuery(id+"F3.opExtrude","SWEPT_FACE",FACE,{"disambiguationData":[OSD([sQuery(id+"F2.wireOp",EDGE,"E8")])]})]}),makeQuery(id+"F7.opExtrude","SWEPT_FACE",FACE,{"disambiguationData":[OSD([sQuery(id+"F6.wireOp",EDGE,"E12.bottom")])]})]}),makeQuery(id+"F10.opExtrude","SWEPT_FACE",FACE,{"disambiguationData":[OSD([sQuery(id+"F9.wireOp",EDGE,"E15.top")])]})]}),makeQuery(id+"F13.opExtrude","SWEPT_FACE",FACE,{"disambiguationData":[OSD([sQuery(id+"F12.wireOp",EDGE,"E18.top")])]})]}),makeQuery(id+"F16.opExtrude","SWEPT_FACE",FACE,{"disambiguationData":[OSD([sQuery(id+"F15.wireOp",EDGE,"E21.top")])]}),makeQuery(id+"F16.opExtrude","SWEPT_FACE",FACE,{"disambiguationData":[OSD([sQuery(id+"F15.wireOp",EDGE,"E24.top")])]})]}),makeQuery(id+"F20.opExtrude","SWEPT_FACE",FACE,{"disambiguationData":[OSD([sQuery(id+"F19.wireOp",EDGE,"E27.top")])]})]}),makeQuery(id+"F28.opExtrude","SWEPT_FACE",FACE,{"disambiguationData":[OSD([sQuery(id+"F27.wireOp",EDGE,"E42.top")])]})]}),makeQuery(id+"F36.opExtrude","SWEPT_FACE",FACE,{"disambiguationData":[OSD([sQuery(id+"F35.wireOp",EDGE,"E52.top")])]})]}),makeQuery(id+"F49.opExtrude","SWEPT_FACE",FACE,{"disambiguationData":[OSD([sQuery(id+"F48.wireOp",EDGE,"E76.top")])]})]}),makeQuery(id+"F51.opExtrude","SWEPT_FACE",FACE,{"disambiguationData":[OSD([sQuery(id+"F50.wireOp",EDGE,"E77.top")])]})]}),makeQuery(id+"F53.opExtrude","SWEPT_FACE",FACE,{"disambiguationData":[OSD([sQuery(id+"F52.wireOp",EDGE,"E78.top")])]})]}),makeQuery(id+"F55.opExtrude","SWEPT_FACE",FACE,{"disambiguationData":[OSD([sQuery(id+"F54.wireOp",EDGE,"E79.bottom")])]})]});
            var sketch = newSketch(context, id + "F66", { "sketchPlane" : qUnion([Q0])});
            skLineSegment(sketch, "E98.bottom", {"start": v(138.14, 394.7) * mm, "end": v(120.36, 394.7) * mm});
            skLineSegment(sketch, "E98.top", {"start": v(138.14, 376.93) * mm, "end": v(120.36, 376.93) * mm});
            skLineSegment(sketch, "E98.left", {"start": v(138.14, 394.7) * mm, "end": v(138.14, 376.93) * mm});
            skLineSegment(sketch, "E98.right", {"start": v(120.36, 394.7) * mm, "end": v(120.36, 376.93) * mm});
            skSolve(sketch);
        }
        {
            var Q0;
            Q0=makeQuery(id+"F66.imprint","IMPRINT",FACE,{"disambiguationData":[TD([[makeQuery(id+"F66.imprint","IMPRINT",EDGE,{"derivedFrom":sQuery(id+"F66.wireOp",EDGE,"E98.bottom")}),1.0]])]});
            extrude(context, id + "F67", {"entities" : qUnion([Q0]), "operationType" : NewBodyOperationType.ADD, "oppositeDirection" : true, "depth" : 114.3 * mm, "offsetDistance" : 25.4 * mm});
        }
        {
            var Q0;
            {var subQ0=sQuery(id+"F2.wireOp",EDGE,"E10");Q0=makeQuery(id+"F16.boolean.opBoolean","MERGE",FACE,{"derivedFrom":[makeQuery(id+"F5.boolean.opBoolean","MERGE",FACE,{"derivedFrom":[makeQuery(id+"F4.boolean.opBoolean","MERGE",FACE,{"derivedFrom":[makeQuery(id+"F3.boolean.opBoolean","MERGE",FACE,{"derivedFrom":[makeQuery(id+"F1.opExtrude","CAP_FACE",FACE,{"disambiguationData":[OSD([sQuery(id+"F0.wireOp",EDGE,"E0"),sQuery(id+"F0.wireOp",EDGE,"E1"),sQuery(id+"F0.wireOp",EDGE,"E3"),sQuery(id+"F0.wireOp",EDGE,"E4"),sQuery(id+"F0.wireOp",EDGE,"E5")])],"isStart":false}),makeQuery(id+"F3.opExtrude","SWEPT_FACE",FACE,{"disambiguationData":[OSD([sQuery(id+"F2.wireOp",EDGE,"E9")])]})]}),makeQuery(id+"F4.opExtrude","SWEPT_FACE",FACE,{"disambiguationData":[OSD([subQ0])]})]}),makeQuery(id+"F5.opExtrude","SWEPT_FACE",FACE,{"disambiguationData":[OSD([subQ0])]})]}),makeQuery(id+"F16.opExtrude","SWEPT_FACE",FACE,{"disambiguationData":[OSD([sQuery(id+"F15.wireOp",EDGE,"E24.left")])]})]});}
            var sketch = newSketch(context, id + "F68", { "sketchPlane" : qUnion([Q0])});
            skLineSegment(sketch, "E99.bottom", {"start": v(76.47, 2.99) * mm, "end": v(101.87, 2.99) * mm});
            skLineSegment(sketch, "E99.top", {"start": v(76.47, 43.63) * mm, "end": v(101.87, 43.63) * mm});
            skLineSegment(sketch, "E99.left", {"start": v(76.47, 2.99) * mm, "end": v(76.47, 43.63) * mm});
            skLineSegment(sketch, "E99.right", {"start": v(101.87, 2.99) * mm, "end": v(101.87, 43.63) * mm});
            skLineSegment(sketch, "E100.bottom", {"start": v(7.71, 51.45) * mm, "end": v(33.11, 51.45) * mm});
            skLineSegment(sketch, "E100.top", {"start": v(7.71, 26.05) * mm, "end": v(33.11, 26.05) * mm});
            skLineSegment(sketch, "E100.left", {"start": v(7.71, 51.45) * mm, "end": v(7.71, 26.05) * mm});
            skLineSegment(sketch, "E100.right", {"start": v(33.11, 51.45) * mm, "end": v(33.11, 26.05) * mm});
            skLineSegment(sketch, "E101.top", {"start": v(-163.12, -19.23) * mm, "end": v(-145.34, -19.23) * mm});
            skLineSegment(sketch, "E102", {"start": v(-163.12, -19.23) * mm, "end": v(-163.12, -37) * mm});
            skLineSegment(sketch, "E103", {"start": v(-163.12, -37) * mm, "end": v(-145.34, -37) * mm});
            skLineSegment(sketch, "E104", {"start": v(-145.34, -37) * mm, "end": v(-145.34, -19.23) * mm});
            skSolve(sketch);
        }
        {
            var Q0;
            Q0=makeQuery(id+"F26.boolean.opBoolean","MERGE",FACE,{"derivedFrom":[makeQuery(id+"F20.boolean.opBoolean","MERGE",FACE,{"derivedFrom":[makeQuery(id+"F16.opExtrude","CAP_FACE",FACE,{"disambiguationData":[OSD([sQuery(id+"F15.wireOp",EDGE,"E21.top"),sQuery(id+"F15.wireOp",EDGE,"E21.left"),sQuery(id+"F15.wireOp",EDGE,"E21.right"),sQuery(id+"F15.wireOp",EDGE,"E22"),sQuery(id+"F15.wireOp",EDGE,"E23")])],"isStart":false}),makeQuery(id+"F16.opExtrude","CAP_FACE",FACE,{"disambiguationData":[OSD([sQuery(id+"F15.wireOp",EDGE,"E24.top"),sQuery(id+"F15.wireOp",EDGE,"E24.left"),sQuery(id+"F15.wireOp",EDGE,"E24.right"),sQuery(id+"F15.wireOp",EDGE,"E25"),sQuery(id+"F15.wireOp",EDGE,"E26")])],"isStart":false}),makeQuery(id+"F20.opExtrude","SWEPT_FACE",FACE,{"disambiguationData":[OSD([sQuery(id+"F19.wireOp",EDGE,"E27.right")])]})]}),makeQuery(id+"F26.opExtrude","CAP_FACE",FACE,{"disambiguationData":[OSD([sQuery(id+"F25.wireOp",EDGE,"E36"),sQuery(id+"F25.wireOp",EDGE,"E37"),sQuery(id+"F25.wireOp",EDGE,"E38")])],"isStart":true}),makeQuery(id+"F26.opExtrude","CAP_FACE",FACE,{"disambiguationData":[OSD([sQuery(id+"F25.wireOp",EDGE,"E39"),sQuery(id+"F25.wireOp",EDGE,"E40"),sQuery(id+"F25.wireOp",EDGE,"E41")])],"isStart":true})]});
            var sketch = newSketch(context, id + "F69", { "sketchPlane" : qUnion([Q0])});
            skLineSegment(sketch, "E105.bottom", {"start": v(346.53, 17.78) * mm, "end": v(364.31, 17.78) * mm});
            skLineSegment(sketch, "E105.top", {"start": v(346.53, 0) * mm, "end": v(364.31, 0) * mm});
            skLineSegment(sketch, "E105.left", {"start": v(346.53, 17.78) * mm, "end": v(346.53, 0) * mm});
            skLineSegment(sketch, "E105.right", {"start": v(364.31, 17.78) * mm, "end": v(364.31, 0) * mm});
            skLineSegment(sketch, "E106.bottom", {"start": v(135.45, 17.78) * mm, "end": v(153.23, 17.78) * mm});
            skLineSegment(sketch, "E106.top", {"start": v(135.45, 0) * mm, "end": v(153.23, 0) * mm});
            skLineSegment(sketch, "E106.left", {"start": v(135.45, 17.78) * mm, "end": v(135.45, 0) * mm});
            skLineSegment(sketch, "E106.right", {"start": v(153.23, 17.78) * mm, "end": v(153.23, 0) * mm});
            skLineSegment(sketch, "E107.bottom", {"start": v(222.36, -50.8) * mm, "end": v(263, -50.8) * mm});
            skLineSegment(sketch, "E107.top", {"start": v(222.36, -15.24) * mm, "end": v(263, -15.24) * mm});
            skLineSegment(sketch, "E107.left", {"start": v(222.36, -50.8) * mm, "end": v(222.36, -15.24) * mm});
            skLineSegment(sketch, "E107.right", {"start": v(263, -50.8) * mm, "end": v(263, -15.24) * mm});
            skLineSegment(sketch, "E108.bottom", {"start": v(239.64, -15.24) * mm, "end": v(242.68, -15.24) * mm});
            skLineSegment(sketch, "E108.top", {"start": v(239.64, -50.8) * mm, "end": v(242.68, -50.8) * mm});
            skLineSegment(sketch, "E108.left", {"start": v(239.64, -15.24) * mm, "end": v(239.64, -50.8) * mm});
            skLineSegment(sketch, "E108.right", {"start": v(242.68, -15.24) * mm, "end": v(242.68, -50.8) * mm});
            skLineSegment(sketch, "E109.bottom", {"start": v(0, -45.72) * mm, "end": v(88.9, -45.72) * mm});
            skLineSegment(sketch, "E109.top", {"start": v(0, -50.8) * mm, "end": v(88.9, -50.8) * mm});
            skLineSegment(sketch, "E109.left", {"start": v(0, -45.72) * mm, "end": v(0, -50.8) * mm});
            skLineSegment(sketch, "E109.right", {"start": v(88.9, -45.72) * mm, "end": v(88.9, -50.8) * mm});
            skLineSegment(sketch, "E110.bottom", {"start": v(29.1, -45.72) * mm, "end": v(49.43, -45.72) * mm});
            skLineSegment(sketch, "E110.top", {"start": v(29.1, -7.62) * mm, "end": v(49.43, -7.62) * mm});
            skLineSegment(sketch, "E110.left", {"start": v(29.1, -45.72) * mm, "end": v(29.1, -7.62) * mm});
            skLineSegment(sketch, "E110.right", {"start": v(49.43, -45.72) * mm, "end": v(49.43, -7.62) * mm});
            skLineSegment(sketch, "E111.bottom", {"start": v(508, -45.72) * mm, "end": v(419.1, -45.72) * mm});
            skLineSegment(sketch, "E111.top", {"start": v(508, -50.8) * mm, "end": v(419.1, -50.8) * mm});
            skLineSegment(sketch, "E111.left", {"start": v(508, -45.72) * mm, "end": v(508, -50.8) * mm});
            skLineSegment(sketch, "E111.right", {"start": v(419.1, -45.72) * mm, "end": v(419.1, -50.8) * mm});
            skLineSegment(sketch, "E112.bottom", {"start": v(450.74, -45.72) * mm, "end": v(471.06, -45.72) * mm});
            skLineSegment(sketch, "E112.top", {"start": v(450.74, -7.62) * mm, "end": v(471.06, -7.62) * mm});
            skLineSegment(sketch, "E112.left", {"start": v(450.74, -45.72) * mm, "end": v(450.74, -7.62) * mm});
            skLineSegment(sketch, "E112.right", {"start": v(471.06, -45.72) * mm, "end": v(471.06, -7.62) * mm});
            skSolve(sketch);
        }
        {
            var Q0;
            Q0=makeQuery(id+"F69.imprint","IMPRINT",FACE,{"disambiguationData":[TD([[makeQuery(id+"F69.imprint","IMPRINT",EDGE,{"derivedFrom":sQuery(id+"F69.wireOp",EDGE,"E109.top")}),-1.0]])]});
            var Q1;
            Q1=makeQuery(id+"F69.imprint","IMPRINT",FACE,{"disambiguationData":[TD([[makeQuery(id+"F69.imprint","IMPRINT",EDGE,{"derivedFrom":sQuery(id+"F69.wireOp",EDGE,"E111.top")}),-1.0]])]});
            extrude(context, id + "F70", {"entities" : qUnion([Q0, Q1]), "operationType" : NewBodyOperationType.ADD, "depth" : 63.5 * mm, "offsetDistance" : 25.4 * mm});
        }
        {
            var Q0;
            Q0=makeQuery(id+"F70.boolean.opBoolean","MERGE",FACE,{"derivedFrom":[makeQuery(id+"F16.boolean.opBoolean","MERGE",FACE,{"derivedFrom":[makeQuery(id+"F10.boolean.opBoolean","MERGE",FACE,{"derivedFrom":[makeQuery(id+"F1.opExtrude","CAP_FACE",FACE,{"disambiguationData":[OSD([sQuery(id+"F0.wireOp",EDGE,"E0"),sQuery(id+"F0.wireOp",EDGE,"E1"),sQuery(id+"F0.wireOp",EDGE,"E3"),sQuery(id+"F0.wireOp",EDGE,"E4"),sQuery(id+"F0.wireOp",EDGE,"E5")])],"isStart":true}),makeQuery(id+"F10.opExtrude","SWEPT_FACE",FACE,{"disambiguationData":[OSD([sQuery(id+"F9.wireOp",EDGE,"E15.right")])]})]}),makeQuery(id+"F16.opExtrude","SWEPT_FACE",FACE,{"disambiguationData":[OSD([sQuery(id+"F15.wireOp",EDGE,"E21.left")])]})]}),makeQuery(id+"F70.opExtrude","SWEPT_FACE",FACE,{"disambiguationData":[OSD([sQuery(id+"F69.wireOp",EDGE,"E109.left")])]})]});
            var sketch = newSketch(context, id + "F71", { "sketchPlane" : qUnion([Q0])});
            skLineSegment(sketch, "E113.bottom", {"start": v(-20.32, -43.18) * mm, "end": v(0, -43.18) * mm});
            skLineSegment(sketch, "E113.top", {"start": v(-20.32, -7.62) * mm, "end": v(0, -7.62) * mm});
            skLineSegment(sketch, "E113.left", {"start": v(-20.32, -43.18) * mm, "end": v(-20.32, -7.62) * mm});
            skLineSegment(sketch, "E113.right", {"start": v(0, -43.18) * mm, "end": v(0, -7.62) * mm});
            skLineSegment(sketch, "E114.bottom", {"start": v(90.3, -7.62) * mm, "end": v(103, -7.62) * mm});
            skLineSegment(sketch, "E114.top", {"start": v(90.3, -20.32) * mm, "end": v(103, -20.32) * mm});
            skLineSegment(sketch, "E114.left", {"start": v(90.3, -7.62) * mm, "end": v(90.3, -20.32) * mm});
            skLineSegment(sketch, "E114.right", {"start": v(103, -7.62) * mm, "end": v(103, -20.32) * mm});
            skLineSegment(sketch, "E115.bottom", {"start": v(186.36, -7.62) * mm, "end": v(199.06, -7.62) * mm});
            skLineSegment(sketch, "E115.top", {"start": v(186.36, -20.32) * mm, "end": v(199.06, -20.32) * mm});
            skLineSegment(sketch, "E115.left", {"start": v(186.36, -7.62) * mm, "end": v(186.36, -20.32) * mm});
            skLineSegment(sketch, "E115.right", {"start": v(199.06, -7.62) * mm, "end": v(199.06, -20.32) * mm});
            skSolve(sketch);
        }
        {
            var Q0;
            Q0=makeQuery(id+"F13.opExtrude","SWEPT_FACE",FACE,{"disambiguationData":[OSD([sQuery(id+"F12.wireOp",EDGE,"E18.left")])]});
            var sketch = newSketch(context, id + "F72", { "sketchPlane" : qUnion([Q0])});
            skLineSegment(sketch, "E116.bottom", {"start": v(-67.42, -14.18) * mm, "end": v(-26.78, -14.18) * mm});
            skLineSegment(sketch, "E116.top", {"start": v(-67.42, -29.42) * mm, "end": v(-26.78, -29.42) * mm});
            skLineSegment(sketch, "E116.left", {"start": v(-67.42, -14.18) * mm, "end": v(-67.42, -29.42) * mm});
            skLineSegment(sketch, "E116.right", {"start": v(-26.78, -14.18) * mm, "end": v(-26.78, -29.42) * mm});
            skSolve(sketch);
        }
        {
            var Q0;
            Q0=makeQuery(id+"F30.boolean.opBoolean","MERGE",FACE,{"derivedFrom":[makeQuery(id+"F28.boolean.opBoolean","MERGE",FACE,{"derivedFrom":[makeQuery(id+"F13.opExtrude","CAP_FACE",FACE,{"disambiguationData":[OSD([sQuery(id+"F12.wireOp",EDGE,"E18.top"),sQuery(id+"F12.wireOp",EDGE,"E18.left"),sQuery(id+"F12.wireOp",EDGE,"E18.right"),sQuery(id+"F12.wireOp",EDGE,"E19"),sQuery(id+"F12.wireOp",EDGE,"E20")])],"isStart":false}),makeQuery(id+"F28.opExtrude","SWEPT_FACE",FACE,{"disambiguationData":[OSD([sQuery(id+"F27.wireOp",EDGE,"E42.left")])]})]}),makeQuery(id+"F30.opExtrude","SWEPT_FACE",FACE,{"disambiguationData":[OSD([sQuery(id+"F29.wireOp",EDGE,"E43.bottom")])]}),makeQuery(id+"F30.opExtrude","SWEPT_FACE",FACE,{"disambiguationData":[OSD([sQuery(id+"F29.wireOp",EDGE,"E45.top")])]})]});
            var sketch = newSketch(context, id + "F73", { "sketchPlane" : qUnion([Q0])});
            skLineSegment(sketch, "E117.bottom", {"start": v(-119.96, 3.46) * mm, "end": v(-86.94, 3.46) * mm});
            skLineSegment(sketch, "E117.top", {"start": v(-119.96, -16.86) * mm, "end": v(-86.94, -16.86) * mm});
            skLineSegment(sketch, "E117.left", {"start": v(-119.96, 3.46) * mm, "end": v(-119.96, -16.86) * mm});
            skLineSegment(sketch, "E117.right", {"start": v(-86.94, 3.46) * mm, "end": v(-86.94, -16.86) * mm});
            skSolve(sketch);
        }
        {
            var Q0;
            Q0=makeQuery(id+"F13.boolean.opBoolean","MERGE",FACE,{"derivedFrom":[makeQuery(id+"F10.opExtrude","CAP_FACE",FACE,{"disambiguationData":[OSD([sQuery(id+"F9.wireOp",EDGE,"E15.top"),sQuery(id+"F9.wireOp",EDGE,"E15.left"),sQuery(id+"F9.wireOp",EDGE,"E15.right"),sQuery(id+"F9.wireOp",EDGE,"E16"),sQuery(id+"F9.wireOp",EDGE,"E17")])],"isStart":false}),makeQuery(id+"F13.opExtrude","SWEPT_FACE",FACE,{"disambiguationData":[OSD([sQuery(id+"F12.wireOp",EDGE,"E18.right")])]})]});
            var sketch = newSketch(context, id + "F74", { "sketchPlane" : qUnion([Q0])});
            skLineSegment(sketch, "E118.bottom", {"start": v(-76.07, -50.8) * mm, "end": v(-55.75, -50.8) * mm});
            skLineSegment(sketch, "E118.top", {"start": v(-76.07, -15.24) * mm, "end": v(-55.75, -15.24) * mm});
            skLineSegment(sketch, "E118.left", {"start": v(-76.07, -50.8) * mm, "end": v(-76.07, -15.24) * mm});
            skLineSegment(sketch, "E118.right", {"start": v(-55.75, -50.8) * mm, "end": v(-55.75, -15.24) * mm});
            skLineSegment(sketch, "E119.bottom", {"start": v(26.55, -11.12) * mm, "end": v(59.57, -11.12) * mm});
            skLineSegment(sketch, "E119.top", {"start": v(26.55, -31.44) * mm, "end": v(59.57, -31.44) * mm});
            skLineSegment(sketch, "E119.left", {"start": v(26.55, -11.12) * mm, "end": v(26.55, -31.44) * mm});
            skLineSegment(sketch, "E119.right", {"start": v(59.57, -11.12) * mm, "end": v(59.57, -31.44) * mm});
            skSolve(sketch);
        }
        {
            var Q0;
            {var subQ2=sQuery(id+"F0.wireOp",EDGE,"E1");var subQ4=sQuery(id+"F6.wireOp",EDGE,"E12.right");Q0=makeQuery(id+"F24.boolean.opBoolean","MERGE",FACE,{"derivedFrom":[makeQuery(id+"F7.boolean.opBoolean","SPLIT",FACE,{"disambiguationData":[TD([makeQuery(id+"F7.opExtrude","SWEPT_FACE",FACE,{"disambiguationData":[OSD([subQ4])]})])],"derivedFrom":makeQuery(id+"F1.opExtrude","SWEPT_FACE",FACE,{"disambiguationData":[OSD([subQ2])]})}),makeQuery(id+"F24.opExtrude","CAP_FACE",FACE,{"disambiguationData":[OSD([sQuery(id+"F23.wireOp",EDGE,"E30"),sQuery(id+"F23.wireOp",EDGE,"E31"),sQuery(id+"F23.wireOp",EDGE,"E32")])],"isStart":false})]});}
            var sketch = newSketch(context, id + "F75", { "sketchPlane" : qUnion([Q0])});
            skLineSegment(sketch, "E120.bottom", {"start": v(-157.57, -6.18) * mm, "end": v(-137.25, -6.18) * mm});
            skLineSegment(sketch, "E120.top", {"start": v(-157.57, -26.5) * mm, "end": v(-137.25, -26.5) * mm});
            skLineSegment(sketch, "E120.left", {"start": v(-157.57, -6.18) * mm, "end": v(-157.57, -26.5) * mm});
            skLineSegment(sketch, "E120.right", {"start": v(-137.25, -6.18) * mm, "end": v(-137.25, -26.5) * mm});
            skLineSegment(sketch, "E121.bottom", {"start": v(-332.79, -9.68) * mm, "end": v(-312.47, -9.68) * mm});
            skLineSegment(sketch, "E121.top", {"start": v(-332.79, -30) * mm, "end": v(-312.47, -30) * mm});
            skLineSegment(sketch, "E121.left", {"start": v(-332.79, -9.68) * mm, "end": v(-332.79, -30) * mm});
            skLineSegment(sketch, "E121.right", {"start": v(-312.47, -9.68) * mm, "end": v(-312.47, -30) * mm});
            skSolve(sketch);
        }
        {
            var Q0;
            Q0=makeQuery(id+"F7.opExtrude","CAP_FACE",FACE,{"disambiguationData":[OSD([sQuery(id+"F6.wireOp",EDGE,"E12.bottom"),sQuery(id+"F6.wireOp",EDGE,"E12.left"),sQuery(id+"F6.wireOp",EDGE,"E12.right"),sQuery(id+"F6.wireOp",EDGE,"E13"),sQuery(id+"F6.wireOp",EDGE,"E14")])],"isStart":false});
            var sketch = newSketch(context, id + "F76", { "sketchPlane" : qUnion([Q0])});
            skLineSegment(sketch, "E122.bottom", {"start": v(-222.28, -50.8) * mm, "end": v(-201.96, -50.8) * mm});
            skLineSegment(sketch, "E122.top", {"start": v(-222.28, -15.24) * mm, "end": v(-201.96, -15.24) * mm});
            skLineSegment(sketch, "E122.left", {"start": v(-222.28, -50.8) * mm, "end": v(-222.28, -15.24) * mm});
            skLineSegment(sketch, "E122.right", {"start": v(-201.96, -50.8) * mm, "end": v(-201.96, -15.24) * mm});
            skSolve(sketch);
        }
        {
            var Q0;
            {var subQ0=sQuery(id+"F2.wireOp",EDGE,"E6");Q0=makeQuery(id+"F4.boolean.opBoolean","MERGE",FACE,{"derivedFrom":[makeQuery(id+"F3.opExtrude","CAP_FACE",FACE,{"disambiguationData":[OSD([subQ0,sQuery(id+"F2.wireOp",EDGE,"E7"),sQuery(id+"F2.wireOp",EDGE,"E8"),sQuery(id+"F2.wireOp",EDGE,"E9")])],"isStart":false}),makeQuery(id+"F4.opExtrude","CAP_FACE",FACE,{"disambiguationData":[OSD([subQ0,sQuery(id+"F2.wireOp",EDGE,"E10"),sQuery(id+"F2.wireOp",EDGE,"E11")])],"isStart":false})]});}
            var sketch = newSketch(context, id + "F77", { "sketchPlane" : qUnion([Q0])});
            skLineSegment(sketch, "E123.bottom", {"start": v(-499.16, 63.15) * mm, "end": v(-478.84, 63.15) * mm});
            skLineSegment(sketch, "E123.top", {"start": v(-499.16, 42.83) * mm, "end": v(-478.84, 42.83) * mm});
            skLineSegment(sketch, "E123.left", {"start": v(-499.16, 63.15) * mm, "end": v(-499.16, 42.83) * mm});
            skLineSegment(sketch, "E123.right", {"start": v(-478.84, 63.15) * mm, "end": v(-478.84, 42.83) * mm});
            skLineSegment(sketch, "E124.bottom", {"start": v(-500.06, 20.32) * mm, "end": v(-479.74, 20.32) * mm});
            skLineSegment(sketch, "E124.top", {"start": v(-500.06, 0) * mm, "end": v(-479.74, 0) * mm});
            skLineSegment(sketch, "E124.left", {"start": v(-500.06, 20.32) * mm, "end": v(-500.06, 0) * mm});
            skLineSegment(sketch, "E124.right", {"start": v(-479.74, 20.32) * mm, "end": v(-479.74, 0) * mm});
            skLineSegment(sketch, "E125.bottom", {"start": v(-500.17, -19.67) * mm, "end": v(-479.85, -19.67) * mm});
            skLineSegment(sketch, "E125.top", {"start": v(-500.17, -39.99) * mm, "end": v(-479.85, -39.99) * mm});
            skLineSegment(sketch, "E125.left", {"start": v(-500.17, -19.67) * mm, "end": v(-500.17, -39.99) * mm});
            skLineSegment(sketch, "E125.right", {"start": v(-479.85, -19.67) * mm, "end": v(-479.85, -39.99) * mm});
            skLineSegment(sketch, "E126.bottom", {"start": v(-418.89, -25.4) * mm, "end": v(-398.57, -25.4) * mm});
            skLineSegment(sketch, "E126.top", {"start": v(-418.89, -50.8) * mm, "end": v(-398.57, -50.8) * mm});
            skLineSegment(sketch, "E126.left", {"start": v(-418.89, -25.4) * mm, "end": v(-418.89, -50.8) * mm});
            skLineSegment(sketch, "E126.right", {"start": v(-398.57, -25.4) * mm, "end": v(-398.57, -50.8) * mm});
            skSolve(sketch);
        }
        {
            var Q0;
            Q0=makeQuery(id+"F69.imprint","IMPRINT",FACE,{"disambiguationData":[TD([[makeQuery(id+"F69.imprint","IMPRINT",EDGE,{"derivedFrom":sQuery(id+"F69.wireOp",EDGE,"E110.bottom")}),1.0]])]});
            var Q1;
            Q1=makeQuery(id+"F69.imprint","IMPRINT",FACE,{"disambiguationData":[TD([[makeQuery(id+"F69.imprint","IMPRINT",EDGE,{"derivedFrom":sQuery(id+"F69.wireOp",EDGE,"E106.bottom")}),-1.0]])]});
            var Q2;
            {var subQ0=sQuery(id+"F69.wireOp",EDGE,"E107.left");Q2=makeQuery(id+"F69.imprint","IMPRINT",FACE,{"disambiguationData":[TD([[makeQuery(id+"F69.imprint","IMPRINT",EDGE,{"derivedFrom":subQ0}),-1.0]])]});}
            var Q3;
            {var subQ0=sQuery(id+"F69.wireOp",EDGE,"E107.right");Q3=makeQuery(id+"F69.imprint","IMPRINT",FACE,{"disambiguationData":[TD([[makeQuery(id+"F69.imprint","IMPRINT",EDGE,{"derivedFrom":subQ0}),1.0]])]});}
            var Q4;
            Q4=makeQuery(id+"F69.imprint","IMPRINT",FACE,{"disambiguationData":[TD([[makeQuery(id+"F69.imprint","IMPRINT",EDGE,{"derivedFrom":sQuery(id+"F69.wireOp",EDGE,"E105.bottom")}),-1.0]])]});
            var Q5;
            Q5=makeQuery(id+"F69.imprint","IMPRINT",FACE,{"disambiguationData":[TD([[makeQuery(id+"F69.imprint","IMPRINT",EDGE,{"derivedFrom":sQuery(id+"F69.wireOp",EDGE,"E112.bottom")}),1.0]])]});
            extrude(context, id + "F78", {"entities" : qUnion([Q0, Q1, Q2, Q3, Q4, Q5]), "operationType" : NewBodyOperationType.REMOVE, "oppositeDirection" : true, "depth" : 12.7 * mm, "offsetDistance" : 25.4 * mm});
        }
        {
            var Q0;
            Q0=makeQuery(id+"F71.imprint","IMPRINT",FACE,{"disambiguationData":[TD([[makeQuery(id+"F71.imprint","IMPRINT",EDGE,{"derivedFrom":sQuery(id+"F71.wireOp",EDGE,"E113.bottom")}),-1.0]])]});
            var Q1;
            Q1=makeQuery(id+"F71.imprint","IMPRINT",FACE,{"disambiguationData":[TD([[makeQuery(id+"F71.imprint","IMPRINT",EDGE,{"derivedFrom":sQuery(id+"F71.wireOp",EDGE,"E114.bottom")}),-1.0]])]});
            var Q2;
            Q2=makeQuery(id+"F71.imprint","IMPRINT",FACE,{"disambiguationData":[TD([[makeQuery(id+"F71.imprint","IMPRINT",EDGE,{"derivedFrom":sQuery(id+"F71.wireOp",EDGE,"E115.bottom")}),-1.0]])]});
            extrude(context, id + "F79", {"entities" : qUnion([Q0, Q1, Q2]), "operationType" : NewBodyOperationType.REMOVE, "oppositeDirection" : true, "depth" : 12.7 * mm, "offsetDistance" : 25.4 * mm});
        }
        {
            var Q0;
            Q0=makeQuery(id+"F72.imprint","IMPRINT",FACE,{"disambiguationData":[TD([[makeQuery(id+"F72.imprint","IMPRINT",EDGE,{"derivedFrom":sQuery(id+"F72.wireOp",EDGE,"E116.bottom")}),-1.0]])]});
            extrude(context, id + "F80", {"entities" : qUnion([Q0]), "operationType" : NewBodyOperationType.REMOVE, "oppositeDirection" : true, "depth" : 12.7 * mm, "offsetDistance" : 25.4 * mm});
        }
        {
            var Q0;
            Q0=makeQuery(id+"F73.imprint","IMPRINT",FACE,{"disambiguationData":[TD([[makeQuery(id+"F73.imprint","IMPRINT",EDGE,{"derivedFrom":sQuery(id+"F73.wireOp",EDGE,"E117.bottom")}),-1.0]])]});
            extrude(context, id + "F81", {"entities" : qUnion([Q0]), "operationType" : NewBodyOperationType.REMOVE, "oppositeDirection" : true, "depth" : 12.7 * mm, "offsetDistance" : 25.4 * mm});
        }
        {
            var Q0;
            Q0=makeQuery(id+"F74.imprint","IMPRINT",FACE,{"disambiguationData":[TD([[makeQuery(id+"F74.imprint","IMPRINT",EDGE,{"derivedFrom":sQuery(id+"F74.wireOp",EDGE,"E118.bottom")}),1.0]])]});
            var Q1;
            Q1=makeQuery(id+"F74.imprint","IMPRINT",FACE,{"disambiguationData":[TD([[makeQuery(id+"F74.imprint","IMPRINT",EDGE,{"derivedFrom":sQuery(id+"F74.wireOp",EDGE,"E119.bottom")}),-1.0]])]});
            extrude(context, id + "F82", {"entities" : qUnion([Q0, Q1]), "operationType" : NewBodyOperationType.REMOVE, "oppositeDirection" : true, "depth" : 12.7 * mm, "offsetDistance" : 25.4 * mm});
        }
        {
            var Q0;
            Q0=makeQuery(id+"F75.imprint","IMPRINT",FACE,{"disambiguationData":[TD([[makeQuery(id+"F75.imprint","IMPRINT",EDGE,{"derivedFrom":sQuery(id+"F75.wireOp",EDGE,"E120.bottom")}),-1.0]])]});
            var Q1;
            Q1=makeQuery(id+"F75.imprint","IMPRINT",FACE,{"disambiguationData":[TD([[makeQuery(id+"F75.imprint","IMPRINT",EDGE,{"derivedFrom":sQuery(id+"F75.wireOp",EDGE,"E121.bottom")}),-1.0]])]});
            extrude(context, id + "F83", {"entities" : qUnion([Q0, Q1]), "operationType" : NewBodyOperationType.REMOVE, "oppositeDirection" : true, "depth" : 12.7 * mm, "offsetDistance" : 25.4 * mm});
        }
        {
            var Q0;
            Q0=makeQuery(id+"F76.imprint","IMPRINT",FACE,{"disambiguationData":[TD([[makeQuery(id+"F76.imprint","IMPRINT",EDGE,{"derivedFrom":sQuery(id+"F76.wireOp",EDGE,"E122.bottom")}),1.0]])]});
            extrude(context, id + "F84", {"entities" : qUnion([Q0]), "operationType" : NewBodyOperationType.REMOVE, "oppositeDirection" : true, "depth" : 12.7 * mm, "offsetDistance" : 25.4 * mm});
        }
        {
            var Q0;
            Q0=makeQuery(id+"F77.imprint","IMPRINT",FACE,{"disambiguationData":[TD([[makeQuery(id+"F77.imprint","IMPRINT",EDGE,{"derivedFrom":sQuery(id+"F77.wireOp",EDGE,"E123.bottom")}),-1.0]])]});
            var Q1;
            Q1=makeQuery(id+"F77.imprint","IMPRINT",FACE,{"disambiguationData":[TD([[makeQuery(id+"F77.imprint","IMPRINT",EDGE,{"derivedFrom":sQuery(id+"F77.wireOp",EDGE,"E124.bottom")}),-1.0]])]});
            var Q2;
            Q2=makeQuery(id+"F77.imprint","IMPRINT",FACE,{"disambiguationData":[TD([[makeQuery(id+"F77.imprint","IMPRINT",EDGE,{"derivedFrom":sQuery(id+"F77.wireOp",EDGE,"E125.bottom")}),-1.0]])]});
            var Q3;
            Q3=makeQuery(id+"F77.imprint","IMPRINT",FACE,{"disambiguationData":[TD([[makeQuery(id+"F77.imprint","IMPRINT",EDGE,{"derivedFrom":sQuery(id+"F77.wireOp",EDGE,"E126.bottom")}),-1.0]])]});
            extrude(context, id + "F85", {"entities" : qUnion([Q0, Q1, Q2, Q3]), "operationType" : NewBodyOperationType.REMOVE, "oppositeDirection" : true, "depth" : 12.7 * mm, "offsetDistance" : 25.4 * mm});
        }
        {
            var Q0;
            Q0=makeQuery(id+"F68.imprint","IMPRINT",FACE,{"disambiguationData":[TD([[makeQuery(id+"F68.imprint","IMPRINT",EDGE,{"derivedFrom":sQuery(id+"F68.wireOp",EDGE,"E101.bottom")}),1.0]])]});
            var Q1;
            Q1=makeQuery(id+"F68.imprint","IMPRINT",FACE,{"disambiguationData":[TD([[makeQuery(id+"F68.imprint","IMPRINT",EDGE,{"derivedFrom":sQuery(id+"F68.wireOp",EDGE,"E100.bottom")}),-1.0]])]});
            var Q2;
            Q2=makeQuery(id+"F68.imprint","IMPRINT",FACE,{"disambiguationData":[TD([[makeQuery(id+"F68.imprint","IMPRINT",EDGE,{"derivedFrom":sQuery(id+"F68.wireOp",EDGE,"E99.bottom")}),1.0]])]});
            extrude(context, id + "F86", {"entities" : qUnion([Q0, Q1, Q2]), "operationType" : NewBodyOperationType.REMOVE, "oppositeDirection" : true, "depth" : 12.7 * mm, "offsetDistance" : 25.4 * mm});
        }
        {
            var Q0;
            Q0=makeQuery(id+"F24.boolean.opBoolean","MERGE",FACE,{"derivedFrom":[makeQuery(id+"F1.opExtrude","SWEPT_FACE",FACE,{"disambiguationData":[OSD([sQuery(id+"F0.wireOp",EDGE,"E3")])]}),makeQuery(id+"F24.opExtrude","CAP_FACE",FACE,{"disambiguationData":[OSD([sQuery(id+"F23.wireOp",EDGE,"E30"),sQuery(id+"F23.wireOp",EDGE,"E31"),sQuery(id+"F23.wireOp",EDGE,"E32")])],"isStart":true}),makeQuery(id+"F24.opExtrude","CAP_FACE",FACE,{"disambiguationData":[OSD([sQuery(id+"F23.wireOp",EDGE,"E33"),sQuery(id+"F23.wireOp",EDGE,"E34"),sQuery(id+"F23.wireOp",EDGE,"E35")])],"isStart":true})]});
            var sketch = newSketch(context, id + "F87", { "sketchPlane" : qUnion([Q0])});
            skLineSegment(sketch, "E127.bottom", {"start": v(128.21, -46.99) * mm, "end": v(148.53, -46.99) * mm});
            skLineSegment(sketch, "E127.top", {"start": v(128.21, -21.59) * mm, "end": v(148.53, -21.59) * mm});
            skLineSegment(sketch, "E127.left", {"start": v(128.21, -46.99) * mm, "end": v(128.21, -21.59) * mm});
            skLineSegment(sketch, "E127.right", {"start": v(148.53, -46.99) * mm, "end": v(148.53, -21.59) * mm});
            skLineSegment(sketch, "E128.bottom", {"start": v(187.31, -10.83) * mm, "end": v(202.55, -10.83) * mm});
            skLineSegment(sketch, "E128.top", {"start": v(187.31, -26.07) * mm, "end": v(202.55, -26.07) * mm});
            skLineSegment(sketch, "E128.left", {"start": v(187.31, -10.83) * mm, "end": v(187.31, -26.07) * mm});
            skLineSegment(sketch, "E128.right", {"start": v(202.55, -10.83) * mm, "end": v(202.55, -26.07) * mm});
            skLineSegment(sketch, "E129.bottom", {"start": v(268.96, -10.83) * mm, "end": v(284.2, -10.83) * mm});
            skLineSegment(sketch, "E129.top", {"start": v(268.96, -26.07) * mm, "end": v(284.2, -26.07) * mm});
            skLineSegment(sketch, "E129.left", {"start": v(268.96, -10.83) * mm, "end": v(268.96, -26.07) * mm});
            skLineSegment(sketch, "E129.right", {"start": v(284.2, -10.83) * mm, "end": v(284.2, -26.07) * mm});
            skLineSegment(sketch, "E130.bottom", {"start": v(323.46, -46.99) * mm, "end": v(343.78, -46.99) * mm});
            skLineSegment(sketch, "E130.top", {"start": v(323.46, -21.59) * mm, "end": v(343.78, -21.59) * mm});
            skLineSegment(sketch, "E130.left", {"start": v(323.46, -46.99) * mm, "end": v(323.46, -21.59) * mm});
            skLineSegment(sketch, "E130.right", {"start": v(343.78, -46.99) * mm, "end": v(343.78, -21.59) * mm});
            skSolve(sketch);
        }
        {
            var Q0;
            Q0=makeQuery(id+"F16.opExtrude","SWEPT_FACE",FACE,{"disambiguationData":[OSD([sQuery(id+"F15.wireOp",EDGE,"E21.right")])]});
            var sketch = newSketch(context, id + "F88", { "sketchPlane" : qUnion([Q0])});
            skLineSegment(sketch, "E131.bottom", {"start": v(-138.9, -19.54) * mm, "end": v(-108.43, -19.54) * mm});
            skLineSegment(sketch, "E131.top", {"start": v(-138.9, -32.24) * mm, "end": v(-108.43, -32.24) * mm});
            skLineSegment(sketch, "E131.left", {"start": v(-138.9, -19.54) * mm, "end": v(-138.9, -32.24) * mm});
            skLineSegment(sketch, "E131.right", {"start": v(-108.43, -19.54) * mm, "end": v(-108.43, -32.24) * mm});
            skSolve(sketch);
        }
        {
            var Q0;
            Q0=makeQuery(id+"F26.boolean.opBoolean","MERGE",FACE,{"derivedFrom":[makeQuery(id+"F20.opExtrude","SWEPT_FACE",FACE,{"disambiguationData":[OSD([sQuery(id+"F19.wireOp",EDGE,"E27.left")])]}),makeQuery(id+"F26.opExtrude","CAP_FACE",FACE,{"disambiguationData":[OSD([sQuery(id+"F25.wireOp",EDGE,"E36"),sQuery(id+"F25.wireOp",EDGE,"E37"),sQuery(id+"F25.wireOp",EDGE,"E38")])],"isStart":false}),makeQuery(id+"F26.opExtrude","CAP_FACE",FACE,{"disambiguationData":[OSD([sQuery(id+"F25.wireOp",EDGE,"E39"),sQuery(id+"F25.wireOp",EDGE,"E40"),sQuery(id+"F25.wireOp",EDGE,"E41")])],"isStart":false})]});
            var sketch = newSketch(context, id + "F89", { "sketchPlane" : qUnion([Q0])});
            skLineSegment(sketch, "E132.bottom", {"start": v(-274.87, -25.4) * mm, "end": v(-259.63, -25.4) * mm});
            skLineSegment(sketch, "E132.top", {"start": v(-274.87, -50.8) * mm, "end": v(-259.63, -50.8) * mm});
            skLineSegment(sketch, "E132.left", {"start": v(-274.87, -25.4) * mm, "end": v(-274.87, -50.8) * mm});
            skLineSegment(sketch, "E132.right", {"start": v(-259.63, -25.4) * mm, "end": v(-259.63, -50.8) * mm});
            skLineSegment(sketch, "E133.bottom", {"start": v(-363.78, 12.7) * mm, "end": v(-351.08, 12.7) * mm});
            skLineSegment(sketch, "E133.top", {"start": v(-363.78, 0) * mm, "end": v(-351.08, 0) * mm});
            skLineSegment(sketch, "E133.left", {"start": v(-363.78, 12.7) * mm, "end": v(-363.78, 0) * mm});
            skLineSegment(sketch, "E133.right", {"start": v(-351.08, 12.7) * mm, "end": v(-351.08, 0) * mm});
            skLineSegment(sketch, "E134.bottom", {"start": v(-152.54, 12.7) * mm, "end": v(-139.84, 12.7) * mm});
            skLineSegment(sketch, "E134.top", {"start": v(-152.54, 0) * mm, "end": v(-139.84, 0) * mm});
            skLineSegment(sketch, "E134.left", {"start": v(-152.54, 12.7) * mm, "end": v(-152.54, 0) * mm});
            skLineSegment(sketch, "E134.right", {"start": v(-139.84, 12.7) * mm, "end": v(-139.84, 0) * mm});
            skSolve(sketch);
        }
        {
            var Q0;
            Q0=makeQuery(id+"F16.opExtrude","SWEPT_FACE",FACE,{"disambiguationData":[OSD([sQuery(id+"F15.wireOp",EDGE,"E24.right")])]});
            var sketch = newSketch(context, id + "F90", { "sketchPlane" : qUnion([Q0])});
            skLineSegment(sketch, "E135.bottom", {"start": v(110.66, -18) * mm, "end": v(141.14, -18) * mm});
            skLineSegment(sketch, "E135.top", {"start": v(110.66, -30.7) * mm, "end": v(141.14, -30.7) * mm});
            skLineSegment(sketch, "E135.left", {"start": v(110.66, -18) * mm, "end": v(110.66, -30.7) * mm});
            skLineSegment(sketch, "E135.right", {"start": v(141.14, -18) * mm, "end": v(141.14, -30.7) * mm});
            skSolve(sketch);
        }
        {
            var Q0;
            Q0=makeQuery(id+"F87.imprint","IMPRINT",FACE,{"disambiguationData":[TD([[makeQuery(id+"F87.imprint","IMPRINT",EDGE,{"derivedFrom":sQuery(id+"F87.wireOp",EDGE,"E127.bottom")}),1.0]])]});
            var Q1;
            Q1=makeQuery(id+"F87.imprint","IMPRINT",FACE,{"disambiguationData":[TD([[makeQuery(id+"F87.imprint","IMPRINT",EDGE,{"derivedFrom":sQuery(id+"F87.wireOp",EDGE,"E128.bottom")}),-1.0]])]});
            var Q2;
            Q2=makeQuery(id+"F87.imprint","IMPRINT",FACE,{"disambiguationData":[TD([[makeQuery(id+"F87.imprint","IMPRINT",EDGE,{"derivedFrom":sQuery(id+"F87.wireOp",EDGE,"E129.bottom")}),-1.0]])]});
            var Q3;
            Q3=makeQuery(id+"F87.imprint","IMPRINT",FACE,{"disambiguationData":[TD([[makeQuery(id+"F87.imprint","IMPRINT",EDGE,{"derivedFrom":sQuery(id+"F87.wireOp",EDGE,"E130.bottom")}),1.0]])]});
            extrude(context, id + "F91", {"entities" : qUnion([Q0, Q1, Q2, Q3]), "operationType" : NewBodyOperationType.REMOVE, "oppositeDirection" : true, "depth" : 12.7 * mm, "offsetDistance" : 25.4 * mm});
        }
        {
            var Q0;
            Q0=makeQuery(id+"F88.imprint","IMPRINT",FACE,{"disambiguationData":[TD([[makeQuery(id+"F88.imprint","IMPRINT",EDGE,{"derivedFrom":sQuery(id+"F88.wireOp",EDGE,"E131.bottom")}),-1.0]])]});
            extrude(context, id + "F92", {"entities" : qUnion([Q0]), "operationType" : NewBodyOperationType.REMOVE, "oppositeDirection" : true, "depth" : 12.7 * mm, "offsetDistance" : 25.4 * mm});
        }
        {
            var Q0;
            Q0=makeQuery(id+"F89.imprint","IMPRINT",FACE,{"disambiguationData":[TD([[makeQuery(id+"F89.imprint","IMPRINT",EDGE,{"derivedFrom":sQuery(id+"F89.wireOp",EDGE,"E133.bottom")}),-1.0]])]});
            var Q1;
            Q1=makeQuery(id+"F89.imprint","IMPRINT",FACE,{"disambiguationData":[TD([[makeQuery(id+"F89.imprint","IMPRINT",EDGE,{"derivedFrom":sQuery(id+"F89.wireOp",EDGE,"E132.bottom")}),-1.0]])]});
            var Q2;
            Q2=makeQuery(id+"F89.imprint","IMPRINT",FACE,{"disambiguationData":[TD([[makeQuery(id+"F89.imprint","IMPRINT",EDGE,{"derivedFrom":sQuery(id+"F89.wireOp",EDGE,"E134.bottom")}),-1.0]])]});
            extrude(context, id + "F93", {"entities" : qUnion([Q0, Q1, Q2]), "operationType" : NewBodyOperationType.REMOVE, "oppositeDirection" : true, "depth" : 12.7 * mm, "offsetDistance" : 25.4 * mm});
        }
        {
            var Q0;
            Q0=makeQuery(id+"F90.imprint","IMPRINT",FACE,{"disambiguationData":[TD([[makeQuery(id+"F90.imprint","IMPRINT",EDGE,{"derivedFrom":sQuery(id+"F90.wireOp",EDGE,"E135.bottom")}),-1.0]])]});
            extrude(context, id + "F94", {"entities" : qUnion([Q0]), "operationType" : NewBodyOperationType.REMOVE, "oppositeDirection" : true, "depth" : 12.7 * mm, "offsetDistance" : 25.4 * mm});
        }
        {
            var Q0;
            {var subQ0=sQuery(id+"F69.wireOp",EDGE,"E110.bottom");Q0=makeQuery(id+"F78.boolean.opBoolean","MERGE",FACE,{"derivedFrom":[makeQuery(id+"F70.opExtrude","SWEPT_FACE",FACE,{"disambiguationData":[OSD([sQuery(id+"F69.wireOp",EDGE,"E109.bottom"),subQ0])]}),makeQuery(id+"F78.opExtrude","SWEPT_FACE",FACE,{"disambiguationData":[OSD([subQ0])]})]});}
            var sketch = newSketch(context, id + "F95", { "sketchPlane" : qUnion([Q0])});
            skLineSegment(sketch, "E136.bottom", {"start": v(-313.7, 0) * mm, "end": v(-317.5, 0) * mm});
            skLineSegment(sketch, "E136.top", {"start": v(-313.7, -3.81) * mm, "end": v(-317.5, -3.81) * mm});
            skLineSegment(sketch, "E136.left", {"start": v(-313.7, 0) * mm, "end": v(-313.7, -3.81) * mm});
            skLineSegment(sketch, "E136.right", {"start": v(-317.5, 0) * mm, "end": v(-317.5, -3.81) * mm});
            skLineSegment(sketch, "E137.bottom", {"start": v(-313.7, -88.9) * mm, "end": v(-317.5, -88.9) * mm});
            skLineSegment(sketch, "E137.top", {"start": v(-313.7, -85.09) * mm, "end": v(-317.5, -85.09) * mm});
            skLineSegment(sketch, "E137.left", {"start": v(-313.7, -88.9) * mm, "end": v(-313.7, -85.09) * mm});
            skLineSegment(sketch, "E137.right", {"start": v(-317.5, -88.9) * mm, "end": v(-317.5, -85.09) * mm});
            skLineSegment(sketch, "E138.bottom", {"start": v(-254, -85.09) * mm, "end": v(-257.8, -85.09) * mm});
            skLineSegment(sketch, "E138.top", {"start": v(-254, -88.9) * mm, "end": v(-257.8, -88.9) * mm});
            skLineSegment(sketch, "E138.left", {"start": v(-254, -85.09) * mm, "end": v(-254, -88.9) * mm});
            skLineSegment(sketch, "E138.right", {"start": v(-257.8, -85.09) * mm, "end": v(-257.8, -88.9) * mm});
            skLineSegment(sketch, "E139.bottom", {"start": v(-254, -3.81) * mm, "end": v(-257.8, -3.81) * mm});
            skLineSegment(sketch, "E139.top", {"start": v(-254, 0) * mm, "end": v(-257.8, 0) * mm});
            skLineSegment(sketch, "E139.left", {"start": v(-254, -3.81) * mm, "end": v(-254, 0) * mm});
            skLineSegment(sketch, "E139.right", {"start": v(-257.8, -3.81) * mm, "end": v(-257.8, 0) * mm});
            skSolve(sketch);
        }
        {
            var Q0;
            Q0=makeQuery(id+"F95.imprint","IMPRINT",FACE,{"disambiguationData":[TD([[makeQuery(id+"F95.imprint","IMPRINT",EDGE,{"derivedFrom":sQuery(id+"F95.wireOp",EDGE,"E136.bottom")}),-1.0]])]});
            var Q1;
            Q1=makeQuery(id+"F95.imprint","IMPRINT",FACE,{"disambiguationData":[TD([[makeQuery(id+"F95.imprint","IMPRINT",EDGE,{"derivedFrom":sQuery(id+"F95.wireOp",EDGE,"E138.bottom")}),1.0]])]});
            var Q2;
            Q2=makeQuery(id+"F95.imprint","IMPRINT",FACE,{"disambiguationData":[TD([[makeQuery(id+"F95.imprint","IMPRINT",EDGE,{"derivedFrom":sQuery(id+"F95.wireOp",EDGE,"E137.bottom")}),1.0]])]});
            var Q3;
            Q3=makeQuery(id+"F95.imprint","IMPRINT",FACE,{"disambiguationData":[TD([[makeQuery(id+"F95.imprint","IMPRINT",EDGE,{"derivedFrom":sQuery(id+"F95.wireOp",EDGE,"E139.bottom")}),-1.0]])]});
            extrude(context, id + "F96", {"entities" : qUnion([Q0, Q1, Q2, Q3]), "operationType" : NewBodyOperationType.ADD, "depth" : 12.7 * mm, "offsetDistance" : 25.4 * mm});
        }
        {
            var Q0;
            Q0=makeQuery(id+"F96.opExtrude","SWEPT_FACE",FACE,{"disambiguationData":[OSD([sQuery(id+"F95.wireOp",EDGE,"E139.right")])]});
            var sketch = newSketch(context, id + "F97", { "sketchPlane" : qUnion([Q0])});
            skLineSegment(sketch, "E140.bottom", {"start": v(1.02, -34.8) * mm, "end": v(2.54, -34.8) * mm});
            skLineSegment(sketch, "E140.top", {"start": v(1.02, -36.32) * mm, "end": v(2.54, -36.32) * mm});
            skLineSegment(sketch, "E140.left", {"start": v(1.02, -34.8) * mm, "end": v(1.02, -36.32) * mm});
            skLineSegment(sketch, "E140.right", {"start": v(2.54, -34.8) * mm, "end": v(2.54, -36.32) * mm});
            skLineSegment(sketch, "E141.bottom", {"start": v(1.02, -38.86) * mm, "end": v(2.54, -38.86) * mm});
            skLineSegment(sketch, "E141.top", {"start": v(1.02, -40.39) * mm, "end": v(2.54, -40.39) * mm});
            skLineSegment(sketch, "E141.left", {"start": v(1.02, -38.86) * mm, "end": v(1.02, -40.39) * mm});
            skLineSegment(sketch, "E141.right", {"start": v(2.54, -38.86) * mm, "end": v(2.54, -40.39) * mm});
            skLineSegment(sketch, "E142.bottom", {"start": v(1.02, -42.93) * mm, "end": v(2.54, -42.93) * mm});
            skLineSegment(sketch, "E142.top", {"start": v(1.02, -44.45) * mm, "end": v(2.54, -44.45) * mm});
            skLineSegment(sketch, "E142.left", {"start": v(1.02, -42.93) * mm, "end": v(1.02, -44.45) * mm});
            skLineSegment(sketch, "E142.right", {"start": v(2.54, -42.93) * mm, "end": v(2.54, -44.45) * mm});
            skSolve(sketch);
        }
        {
            var Q0;
            Q0=makeQuery(id+"F96.opExtrude","SWEPT_FACE",FACE,{"disambiguationData":[OSD([sQuery(id+"F95.wireOp",EDGE,"E138.right")])]});
            var sketch = newSketch(context, id + "F98", { "sketchPlane" : qUnion([Q0])});
            skLineSegment(sketch, "E143.bottom", {"start": v(86.1, -34.8) * mm, "end": v(87.63, -34.8) * mm});
            skLineSegment(sketch, "E143.top", {"start": v(86.1, -36.32) * mm, "end": v(87.63, -36.32) * mm});
            skLineSegment(sketch, "E143.left", {"start": v(86.1, -34.8) * mm, "end": v(86.1, -36.32) * mm});
            skLineSegment(sketch, "E143.right", {"start": v(87.63, -34.8) * mm, "end": v(87.63, -36.32) * mm});
            skLineSegment(sketch, "E144.bottom", {"start": v(86.1, -38.86) * mm, "end": v(87.63, -38.86) * mm});
            skLineSegment(sketch, "E144.top", {"start": v(86.1, -40.39) * mm, "end": v(87.63, -40.39) * mm});
            skLineSegment(sketch, "E144.left", {"start": v(86.1, -38.86) * mm, "end": v(86.1, -40.39) * mm});
            skLineSegment(sketch, "E144.right", {"start": v(87.63, -38.86) * mm, "end": v(87.63, -40.39) * mm});
            skLineSegment(sketch, "E145.bottom", {"start": v(86.1, -42.93) * mm, "end": v(87.63, -42.93) * mm});
            skLineSegment(sketch, "E145.top", {"start": v(86.1, -44.45) * mm, "end": v(87.63, -44.45) * mm});
            skLineSegment(sketch, "E145.left", {"start": v(86.1, -42.93) * mm, "end": v(86.1, -44.45) * mm});
            skLineSegment(sketch, "E145.right", {"start": v(87.63, -42.93) * mm, "end": v(87.63, -44.45) * mm});
            skSolve(sketch);
        }
        {
            var Q0;
            Q0=makeQuery(id+"F96.opExtrude","SWEPT_FACE",FACE,{"disambiguationData":[OSD([sQuery(id+"F95.wireOp",EDGE,"E136.top")])]});
            var sketch = newSketch(context, id + "F99", { "sketchPlane" : qUnion([Q0])});
            skLineSegment(sketch, "E146.bottom", {"start": v(-316.48, -34.8) * mm, "end": v(-314.96, -34.8) * mm});
            skLineSegment(sketch, "E146.top", {"start": v(-316.48, -36.32) * mm, "end": v(-314.96, -36.32) * mm});
            skLineSegment(sketch, "E146.left", {"start": v(-316.48, -34.8) * mm, "end": v(-316.48, -36.32) * mm});
            skLineSegment(sketch, "E146.right", {"start": v(-314.96, -34.8) * mm, "end": v(-314.96, -36.32) * mm});
            skLineSegment(sketch, "E147.bottom", {"start": v(-316.48, -38.86) * mm, "end": v(-314.96, -38.86) * mm});
            skLineSegment(sketch, "E147.top", {"start": v(-316.48, -40.39) * mm, "end": v(-314.96, -40.39) * mm});
            skLineSegment(sketch, "E147.left", {"start": v(-316.48, -38.86) * mm, "end": v(-316.48, -40.39) * mm});
            skLineSegment(sketch, "E147.right", {"start": v(-314.96, -38.86) * mm, "end": v(-314.96, -40.39) * mm});
            skLineSegment(sketch, "E148.bottom", {"start": v(-316.48, -42.93) * mm, "end": v(-314.96, -42.93) * mm});
            skLineSegment(sketch, "E148.top", {"start": v(-316.48, -44.45) * mm, "end": v(-314.96, -44.45) * mm});
            skLineSegment(sketch, "E148.left", {"start": v(-316.48, -42.93) * mm, "end": v(-316.48, -44.45) * mm});
            skLineSegment(sketch, "E148.right", {"start": v(-314.96, -42.93) * mm, "end": v(-314.96, -44.45) * mm});
            skSolve(sketch);
        }
        {
            var Q0;
            Q0=makeQuery(id+"F97.imprint","IMPRINT",FACE,{"disambiguationData":[TD([[makeQuery(id+"F97.imprint","IMPRINT",EDGE,{"derivedFrom":sQuery(id+"F97.wireOp",EDGE,"E140.bottom")}),-1.0]])]});
            var Q1;
            Q1=makeQuery(id+"F97.imprint","IMPRINT",FACE,{"disambiguationData":[TD([[makeQuery(id+"F97.imprint","IMPRINT",EDGE,{"derivedFrom":sQuery(id+"F97.wireOp",EDGE,"E141.bottom")}),-1.0]])]});
            var Q2;
            Q2=makeQuery(id+"F97.imprint","IMPRINT",FACE,{"disambiguationData":[TD([[makeQuery(id+"F97.imprint","IMPRINT",EDGE,{"derivedFrom":sQuery(id+"F97.wireOp",EDGE,"E142.bottom")}),-1.0]])]});
            extrude(context, id + "F100", {"entities" : qUnion([Q0, Q1, Q2]), "operationType" : NewBodyOperationType.ADD, "depth" : 58.42 * mm, "offsetDistance" : 25.4 * mm});
        }
        {
            var Q0;
            Q0=makeQuery(id+"F99.imprint","IMPRINT",FACE,{"disambiguationData":[TD([[makeQuery(id+"F99.imprint","IMPRINT",EDGE,{"derivedFrom":sQuery(id+"F99.wireOp",EDGE,"E146.bottom")}),-1.0]])]});
            var Q1;
            Q1=makeQuery(id+"F99.imprint","IMPRINT",FACE,{"disambiguationData":[TD([[makeQuery(id+"F99.imprint","IMPRINT",EDGE,{"derivedFrom":sQuery(id+"F99.wireOp",EDGE,"E147.bottom")}),-1.0]])]});
            var Q2;
            Q2=makeQuery(id+"F99.imprint","IMPRINT",FACE,{"disambiguationData":[TD([[makeQuery(id+"F99.imprint","IMPRINT",EDGE,{"derivedFrom":sQuery(id+"F99.wireOp",EDGE,"E148.bottom")}),-1.0]])]});
            extrude(context, id + "F101", {"entities" : qUnion([Q0, Q1, Q2]), "operationType" : NewBodyOperationType.ADD, "depth" : 81.28 * mm, "offsetDistance" : 25.4 * mm});
        }
        {
            var Q0;
            Q0=makeQuery(id+"F98.imprint","IMPRINT",FACE,{"disambiguationData":[TD([[makeQuery(id+"F98.imprint","IMPRINT",EDGE,{"derivedFrom":sQuery(id+"F98.wireOp",EDGE,"E143.bottom")}),-1.0]])]});
            var Q1;
            Q1=makeQuery(id+"F98.imprint","IMPRINT",FACE,{"disambiguationData":[TD([[makeQuery(id+"F98.imprint","IMPRINT",EDGE,{"derivedFrom":sQuery(id+"F98.wireOp",EDGE,"E144.bottom")}),-1.0]])]});
            var Q2;
            Q2=makeQuery(id+"F98.imprint","IMPRINT",FACE,{"disambiguationData":[TD([[makeQuery(id+"F98.imprint","IMPRINT",EDGE,{"derivedFrom":sQuery(id+"F98.wireOp",EDGE,"E145.bottom")}),-1.0]])]});
            extrude(context, id + "F102", {"entities" : qUnion([Q0, Q1, Q2]), "operationType" : NewBodyOperationType.ADD, "depth" : 58.42 * mm, "offsetDistance" : 25.4 * mm});
        }
        {
            var Q0;
            {var subQ0=sQuery(id+"F69.wireOp",EDGE,"E112.bottom");Q0=makeQuery(id+"F78.boolean.opBoolean","MERGE",FACE,{"derivedFrom":[makeQuery(id+"F70.opExtrude","SWEPT_FACE",FACE,{"disambiguationData":[OSD([sQuery(id+"F69.wireOp",EDGE,"E111.bottom"),subQ0])]}),makeQuery(id+"F78.opExtrude","SWEPT_FACE",FACE,{"disambiguationData":[OSD([subQ0])]})]});}
            var sketch = newSketch(context, id + "F103", { "sketchPlane" : qUnion([Q0])});
            skLineSegment(sketch, "E149.bottom", {"start": v(-313.7, -419.1) * mm, "end": v(-317.5, -419.1) * mm});
            skLineSegment(sketch, "E149.top", {"start": v(-313.7, -422.91) * mm, "end": v(-317.5, -422.91) * mm});
            skLineSegment(sketch, "E149.left", {"start": v(-313.7, -419.1) * mm, "end": v(-313.7, -422.91) * mm});
            skLineSegment(sketch, "E149.right", {"start": v(-317.5, -419.1) * mm, "end": v(-317.5, -422.91) * mm});
            skLineSegment(sketch, "E150.bottom", {"start": v(-313.7, -508) * mm, "end": v(-317.5, -508) * mm});
            skLineSegment(sketch, "E150.top", {"start": v(-313.7, -504.2) * mm, "end": v(-317.5, -504.2) * mm});
            skLineSegment(sketch, "E150.left", {"start": v(-313.7, -508) * mm, "end": v(-313.7, -504.2) * mm});
            skLineSegment(sketch, "E150.right", {"start": v(-317.5, -508) * mm, "end": v(-317.5, -504.2) * mm});
            skLineSegment(sketch, "E151.bottom", {"start": v(-257.8, -508) * mm, "end": v(-254, -508) * mm});
            skLineSegment(sketch, "E151.top", {"start": v(-257.8, -504.2) * mm, "end": v(-254, -504.2) * mm});
            skLineSegment(sketch, "E151.left", {"start": v(-257.8, -508) * mm, "end": v(-257.8, -504.2) * mm});
            skLineSegment(sketch, "E151.right", {"start": v(-254, -508) * mm, "end": v(-254, -504.2) * mm});
            skLineSegment(sketch, "E152.bottom", {"start": v(-257.8, -419.1) * mm, "end": v(-254, -419.1) * mm});
            skLineSegment(sketch, "E152.top", {"start": v(-257.8, -422.91) * mm, "end": v(-254, -422.91) * mm});
            skLineSegment(sketch, "E152.left", {"start": v(-257.8, -419.1) * mm, "end": v(-257.8, -422.91) * mm});
            skLineSegment(sketch, "E152.right", {"start": v(-254, -419.1) * mm, "end": v(-254, -422.91) * mm});
            skSolve(sketch);
        }
        {
            var Q0;
            Q0=makeQuery(id+"F103.imprint","IMPRINT",FACE,{"disambiguationData":[TD([[makeQuery(id+"F103.imprint","IMPRINT",EDGE,{"derivedFrom":sQuery(id+"F103.wireOp",EDGE,"E149.bottom")}),-1.0]])]});
            var Q1;
            Q1=makeQuery(id+"F103.imprint","IMPRINT",FACE,{"disambiguationData":[TD([[makeQuery(id+"F103.imprint","IMPRINT",EDGE,{"derivedFrom":sQuery(id+"F103.wireOp",EDGE,"E152.bottom")}),-1.0]])]});
            var Q2;
            Q2=makeQuery(id+"F103.imprint","IMPRINT",FACE,{"disambiguationData":[TD([[makeQuery(id+"F103.imprint","IMPRINT",EDGE,{"derivedFrom":sQuery(id+"F103.wireOp",EDGE,"E150.bottom")}),1.0]])]});
            var Q3;
            Q3=makeQuery(id+"F103.imprint","IMPRINT",FACE,{"disambiguationData":[TD([[makeQuery(id+"F103.imprint","IMPRINT",EDGE,{"derivedFrom":sQuery(id+"F103.wireOp",EDGE,"E151.bottom")}),1.0]])]});
            extrude(context, id + "F104", {"entities" : qUnion([Q0, Q1, Q2, Q3]), "operationType" : NewBodyOperationType.ADD, "depth" : 12.7 * mm, "offsetDistance" : 25.4 * mm});
        }
        {
            var Q0;
            Q0=makeQuery(id+"F104.opExtrude","SWEPT_FACE",FACE,{"disambiguationData":[OSD([sQuery(id+"F103.wireOp",EDGE,"E152.left")])]});
            var sketch = newSketch(context, id + "F105", { "sketchPlane" : qUnion([Q0])});
            skLineSegment(sketch, "E153.bottom", {"start": v(420.12, -34.8) * mm, "end": v(421.64, -34.8) * mm});
            skLineSegment(sketch, "E153.top", {"start": v(420.12, -36.32) * mm, "end": v(421.64, -36.32) * mm});
            skLineSegment(sketch, "E153.left", {"start": v(420.12, -34.8) * mm, "end": v(420.12, -36.32) * mm});
            skLineSegment(sketch, "E153.right", {"start": v(421.64, -34.8) * mm, "end": v(421.64, -36.32) * mm});
            skLineSegment(sketch, "E154.bottom", {"start": v(420.12, -38.86) * mm, "end": v(421.64, -38.86) * mm});
            skLineSegment(sketch, "E154.top", {"start": v(420.12, -40.39) * mm, "end": v(421.64, -40.39) * mm});
            skLineSegment(sketch, "E154.left", {"start": v(420.12, -38.86) * mm, "end": v(420.12, -40.39) * mm});
            skLineSegment(sketch, "E154.right", {"start": v(421.64, -38.86) * mm, "end": v(421.64, -40.39) * mm});
            skLineSegment(sketch, "E155.bottom", {"start": v(420.12, -42.93) * mm, "end": v(421.64, -42.93) * mm});
            skLineSegment(sketch, "E155.top", {"start": v(420.12, -44.45) * mm, "end": v(421.64, -44.45) * mm});
            skLineSegment(sketch, "E155.left", {"start": v(420.12, -42.93) * mm, "end": v(420.12, -44.45) * mm});
            skLineSegment(sketch, "E155.right", {"start": v(421.64, -42.93) * mm, "end": v(421.64, -44.45) * mm});
            skSolve(sketch);
        }
        {
            var Q0;
            Q0=makeQuery(id+"F104.opExtrude","SWEPT_FACE",FACE,{"disambiguationData":[OSD([sQuery(id+"F103.wireOp",EDGE,"E149.top")])]});
            var sketch = newSketch(context, id + "F106", { "sketchPlane" : qUnion([Q0])});
            skLineSegment(sketch, "E156.bottom", {"start": v(-316.48, -34.8) * mm, "end": v(-314.96, -34.8) * mm});
            skLineSegment(sketch, "E156.top", {"start": v(-316.48, -36.32) * mm, "end": v(-314.96, -36.32) * mm});
            skLineSegment(sketch, "E156.left", {"start": v(-316.48, -34.8) * mm, "end": v(-316.48, -36.32) * mm});
            skLineSegment(sketch, "E156.right", {"start": v(-314.96, -34.8) * mm, "end": v(-314.96, -36.32) * mm});
            skLineSegment(sketch, "E157.bottom", {"start": v(-316.48, -38.86) * mm, "end": v(-314.96, -38.86) * mm});
            skLineSegment(sketch, "E157.top", {"start": v(-316.48, -40.39) * mm, "end": v(-314.96, -40.39) * mm});
            skLineSegment(sketch, "E157.left", {"start": v(-316.48, -38.86) * mm, "end": v(-316.48, -40.39) * mm});
            skLineSegment(sketch, "E157.right", {"start": v(-314.96, -38.86) * mm, "end": v(-314.96, -40.39) * mm});
            skLineSegment(sketch, "E158.bottom", {"start": v(-316.48, -42.93) * mm, "end": v(-314.96, -42.93) * mm});
            skLineSegment(sketch, "E158.top", {"start": v(-316.48, -44.45) * mm, "end": v(-314.96, -44.45) * mm});
            skLineSegment(sketch, "E158.left", {"start": v(-316.48, -42.93) * mm, "end": v(-316.48, -44.45) * mm});
            skLineSegment(sketch, "E158.right", {"start": v(-314.96, -42.93) * mm, "end": v(-314.96, -44.45) * mm});
            skSolve(sketch);
        }
        {
            var Q0;
            Q0=makeQuery(id+"F104.opExtrude","SWEPT_FACE",FACE,{"disambiguationData":[OSD([sQuery(id+"F103.wireOp",EDGE,"E151.left")])]});
            var sketch = newSketch(context, id + "F107", { "sketchPlane" : qUnion([Q0])});
            skLineSegment(sketch, "E159.bottom", {"start": v(505.2, -34.8) * mm, "end": v(506.73, -34.8) * mm});
            skLineSegment(sketch, "E159.top", {"start": v(505.2, -36.32) * mm, "end": v(506.73, -36.32) * mm});
            skLineSegment(sketch, "E159.left", {"start": v(505.2, -34.8) * mm, "end": v(505.2, -36.32) * mm});
            skLineSegment(sketch, "E159.right", {"start": v(506.73, -34.8) * mm, "end": v(506.73, -36.32) * mm});
            skLineSegment(sketch, "E160.bottom", {"start": v(505.2, -38.86) * mm, "end": v(506.73, -38.86) * mm});
            skLineSegment(sketch, "E160.top", {"start": v(505.2, -40.39) * mm, "end": v(506.73, -40.39) * mm});
            skLineSegment(sketch, "E160.left", {"start": v(505.2, -38.86) * mm, "end": v(505.2, -40.39) * mm});
            skLineSegment(sketch, "E160.right", {"start": v(506.73, -38.86) * mm, "end": v(506.73, -40.39) * mm});
            skLineSegment(sketch, "E161.bottom", {"start": v(505.2, -42.93) * mm, "end": v(506.73, -42.93) * mm});
            skLineSegment(sketch, "E161.top", {"start": v(505.2, -44.45) * mm, "end": v(506.73, -44.45) * mm});
            skLineSegment(sketch, "E161.left", {"start": v(505.2, -42.93) * mm, "end": v(505.2, -44.45) * mm});
            skLineSegment(sketch, "E161.right", {"start": v(506.73, -42.93) * mm, "end": v(506.73, -44.45) * mm});
            skSolve(sketch);
        }
        {
            var Q0;
            Q0=makeQuery(id+"F105.imprint","IMPRINT",FACE,{"disambiguationData":[TD([[makeQuery(id+"F105.imprint","IMPRINT",EDGE,{"derivedFrom":sQuery(id+"F105.wireOp",EDGE,"E153.bottom")}),-1.0]])]});
            var Q1;
            Q1=makeQuery(id+"F105.imprint","IMPRINT",FACE,{"disambiguationData":[TD([[makeQuery(id+"F105.imprint","IMPRINT",EDGE,{"derivedFrom":sQuery(id+"F105.wireOp",EDGE,"E154.bottom")}),-1.0]])]});
            var Q2;
            Q2=makeQuery(id+"F105.imprint","IMPRINT",FACE,{"disambiguationData":[TD([[makeQuery(id+"F105.imprint","IMPRINT",EDGE,{"derivedFrom":sQuery(id+"F105.wireOp",EDGE,"E155.bottom")}),-1.0]])]});
            extrude(context, id + "F108", {"entities" : qUnion([Q0, Q1, Q2]), "operationType" : NewBodyOperationType.ADD, "depth" : 58.42 * mm, "offsetDistance" : 25.4 * mm});
        }
        {
            var Q0;
            Q0=makeQuery(id+"F106.imprint","IMPRINT",FACE,{"disambiguationData":[TD([[makeQuery(id+"F106.imprint","IMPRINT",EDGE,{"derivedFrom":sQuery(id+"F106.wireOp",EDGE,"E156.bottom")}),-1.0]])]});
            var Q1;
            Q1=makeQuery(id+"F106.imprint","IMPRINT",FACE,{"disambiguationData":[TD([[makeQuery(id+"F106.imprint","IMPRINT",EDGE,{"derivedFrom":sQuery(id+"F106.wireOp",EDGE,"E157.bottom")}),-1.0]])]});
            var Q2;
            Q2=makeQuery(id+"F106.imprint","IMPRINT",FACE,{"disambiguationData":[TD([[makeQuery(id+"F106.imprint","IMPRINT",EDGE,{"derivedFrom":sQuery(id+"F106.wireOp",EDGE,"E158.bottom")}),-1.0]])]});
            extrude(context, id + "F109", {"entities" : qUnion([Q0, Q1, Q2]), "operationType" : NewBodyOperationType.ADD, "depth" : 83.82 * mm, "offsetDistance" : 25.4 * mm});
        }
        {
            var Q0;
            Q0=makeQuery(id+"F107.imprint","IMPRINT",FACE,{"disambiguationData":[TD([[makeQuery(id+"F107.imprint","IMPRINT",EDGE,{"derivedFrom":sQuery(id+"F107.wireOp",EDGE,"E159.bottom")}),-1.0]])]});
            var Q1;
            Q1=makeQuery(id+"F107.imprint","IMPRINT",FACE,{"disambiguationData":[TD([[makeQuery(id+"F107.imprint","IMPRINT",EDGE,{"derivedFrom":sQuery(id+"F107.wireOp",EDGE,"E160.bottom")}),-1.0]])]});
            var Q2;
            Q2=makeQuery(id+"F107.imprint","IMPRINT",FACE,{"disambiguationData":[TD([[makeQuery(id+"F107.imprint","IMPRINT",EDGE,{"derivedFrom":sQuery(id+"F107.wireOp",EDGE,"E161.bottom")}),-1.0]])]});
            extrude(context, id + "F110", {"entities" : qUnion([Q0, Q1, Q2]), "operationType" : NewBodyOperationType.ADD, "depth" : 58.42 * mm, "offsetDistance" : 25.4 * mm});
        }
        {
            var Q0;
            Q0=makeQuery(id+"F39.opExtrude","SWEPT_FACE",FACE,{"disambiguationData":[OSD([sQuery(id+"F37.wireOp",EDGE,"E62.top")])]});
            var sketch = newSketch(context, id + "F111", { "sketchPlane" : qUnion([Q0])});
            skLineSegment(sketch, "E162.bottom", {"start": v(36.83, 558.8) * mm, "end": v(31.75, 558.8) * mm});
            skLineSegment(sketch, "E162.top", {"start": v(36.83, 553.72) * mm, "end": v(31.75, 553.72) * mm});
            skLineSegment(sketch, "E162.left", {"start": v(36.83, 558.8) * mm, "end": v(36.83, 553.72) * mm});
            skLineSegment(sketch, "E162.right", {"start": v(31.75, 558.8) * mm, "end": v(31.75, 553.72) * mm});
            skLineSegment(sketch, "E163.bottom", {"start": v(177.8, 553.72) * mm, "end": v(172.72, 553.72) * mm});
            skLineSegment(sketch, "E163.top", {"start": v(177.8, 558.8) * mm, "end": v(172.72, 558.8) * mm});
            skLineSegment(sketch, "E163.left", {"start": v(177.8, 553.72) * mm, "end": v(177.8, 558.8) * mm});
            skLineSegment(sketch, "E163.right", {"start": v(172.72, 553.72) * mm, "end": v(172.72, 558.8) * mm});
            skSolve(sketch);
        }
        {
            var Q0;
            Q0=makeQuery(id+"F111.imprint","IMPRINT",FACE,{"disambiguationData":[TD([[makeQuery(id+"F111.imprint","IMPRINT",EDGE,{"derivedFrom":sQuery(id+"F111.wireOp",EDGE,"E163.bottom")}),-1.0]])]});
            var Q1;
            Q1=makeQuery(id+"F111.imprint","IMPRINT",FACE,{"disambiguationData":[TD([[makeQuery(id+"F111.imprint","IMPRINT",EDGE,{"derivedFrom":sQuery(id+"F111.wireOp",EDGE,"E162.bottom")}),-1.0]])]});
            extrude(context, id + "F112", {"entities" : qUnion([Q0, Q1]), "operationType" : NewBodyOperationType.ADD, "depth" : 48.26 * mm, "offsetDistance" : 25.4 * mm});
        }
        {
            var Q0;
            Q0=makeQuery(id+"F68.imprint","IMPRINT",FACE,{"disambiguationData":[TD([[makeQuery(id+"F68.imprint","IMPRINT",EDGE,{"derivedFrom":sQuery(id+"F68.wireOp",EDGE,"E101.top")}),-1.0]])]});
            extrude(context, id + "F113", {"entities" : qUnion([Q0]), "operationType" : NewBodyOperationType.REMOVE, "oppositeDirection" : true, "depth" : 12.7 * mm, "offsetDistance" : 25.4 * mm});
        }
    });
